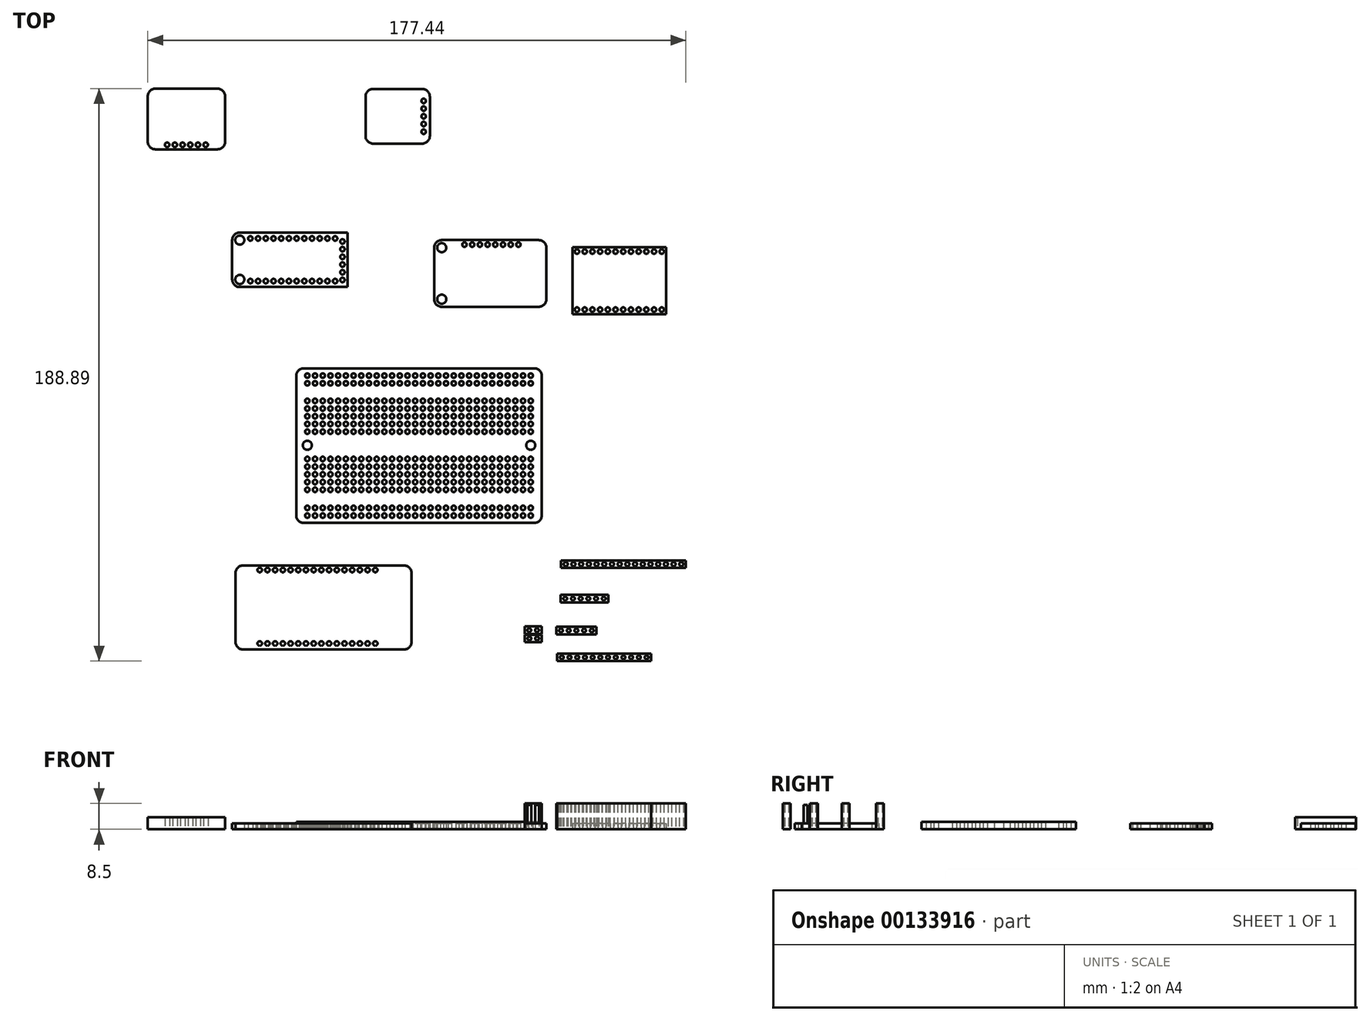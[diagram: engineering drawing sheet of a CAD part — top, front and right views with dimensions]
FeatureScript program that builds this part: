
annotation { "Feature Type Name" : "Feature", "Feature Type Description" : "" }
export const myFeature = defineFeature(function(context is Context, id is Id, definition is map)
    precondition{}
    {
        {
            var Q0;
            Q0=qCreatedBy(makeId("Top.planeOp"),FACE);
            var sketch = newSketch(context, id + "F0", { "sketchPlane" : qUnion([Q0])});
            skLineSegment(sketch, "E0.bottom", {"start": v(-38.07, -25.59) * mm, "end": v(42.93, -25.59) * mm});
            skLineSegment(sketch, "E0.top", {"start": v(-38.07, 25.41) * mm, "end": v(42.93, 25.41) * mm});
            skLineSegment(sketch, "E0.left", {"start": v(-38.07, -25.59) * mm, "end": v(-38.07, 25.41) * mm});
            skLineSegment(sketch, "E0.right", {"start": v(42.93, -25.59) * mm, "end": v(42.93, 25.41) * mm});
            skCircle(sketch, "E1", {"center": v(-34.4, -23.19) * mm, "radius": 0.75 * mm});
            skCircle(sketch, "E2.0.1.0", {"center": v(-34.4, -20.65) * mm, "radius": 0.75 * mm});
            skCircle(sketch, "E2.1.0.0", {"center": v(-31.86, -23.19) * mm, "radius": 0.75 * mm});
            skCircle(sketch, "E2.1.1.0", {"center": v(-31.86, -20.65) * mm, "radius": 0.75 * mm});
            skCircle(sketch, "E2.2.0.0", {"center": v(-29.32, -23.19) * mm, "radius": 0.75 * mm});
            skCircle(sketch, "E2.2.1.0", {"center": v(-29.32, -20.65) * mm, "radius": 0.75 * mm});
            skCircle(sketch, "E2.3.0.0", {"center": v(-26.78, -23.19) * mm, "radius": 0.75 * mm});
            skCircle(sketch, "E2.3.1.0", {"center": v(-26.78, -20.65) * mm, "radius": 0.75 * mm});
            skCircle(sketch, "E2.4.0.0", {"center": v(-24.24, -23.19) * mm, "radius": 0.75 * mm});
            skCircle(sketch, "E2.4.1.0", {"center": v(-24.24, -20.65) * mm, "radius": 0.75 * mm});
            skCircle(sketch, "E2.5.0.0", {"center": v(-21.7, -23.19) * mm, "radius": 0.75 * mm});
            skCircle(sketch, "E2.5.1.0", {"center": v(-21.7, -20.65) * mm, "radius": 0.75 * mm});
            skCircle(sketch, "E2.6.0.0", {"center": v(-19.16, -23.19) * mm, "radius": 0.75 * mm});
            skCircle(sketch, "E2.6.1.0", {"center": v(-19.16, -20.65) * mm, "radius": 0.75 * mm});
            skCircle(sketch, "E2.7.0.0", {"center": v(-16.62, -23.19) * mm, "radius": 0.75 * mm});
            skCircle(sketch, "E2.7.1.0", {"center": v(-16.62, -20.65) * mm, "radius": 0.75 * mm});
            skCircle(sketch, "E2.8.0.0", {"center": v(-14.08, -23.19) * mm, "radius": 0.75 * mm});
            skCircle(sketch, "E2.8.1.0", {"center": v(-14.08, -20.65) * mm, "radius": 0.75 * mm});
            skCircle(sketch, "E2.9.0.0", {"center": v(-11.54, -23.19) * mm, "radius": 0.75 * mm});
            skCircle(sketch, "E2.9.1.0", {"center": v(-11.54, -20.65) * mm, "radius": 0.75 * mm});
            skCircle(sketch, "E2.10.0.0", {"center": v(-9, -23.19) * mm, "radius": 0.75 * mm});
            skCircle(sketch, "E2.10.1.0", {"center": v(-9, -20.65) * mm, "radius": 0.75 * mm});
            skCircle(sketch, "E2.11.0.0", {"center": v(-6.46, -23.19) * mm, "radius": 0.75 * mm});
            skCircle(sketch, "E2.11.1.0", {"center": v(-6.46, -20.65) * mm, "radius": 0.75 * mm});
            skCircle(sketch, "E2.12.0.0", {"center": v(-3.92, -23.19) * mm, "radius": 0.75 * mm});
            skCircle(sketch, "E2.12.1.0", {"center": v(-3.92, -20.65) * mm, "radius": 0.75 * mm});
            skCircle(sketch, "E2.13.0.0", {"center": v(-1.38, -23.19) * mm, "radius": 0.75 * mm});
            skCircle(sketch, "E2.13.1.0", {"center": v(-1.38, -20.65) * mm, "radius": 0.75 * mm});
            skCircle(sketch, "E2.14.0.0", {"center": v(1.16, -23.19) * mm, "radius": 0.75 * mm});
            skCircle(sketch, "E2.14.1.0", {"center": v(1.16, -20.65) * mm, "radius": 0.75 * mm});
            skCircle(sketch, "E2.15.0.0", {"center": v(3.7, -23.19) * mm, "radius": 0.75 * mm});
            skCircle(sketch, "E2.15.1.0", {"center": v(3.7, -20.65) * mm, "radius": 0.75 * mm});
            skCircle(sketch, "E2.16.0.0", {"center": v(6.24, -23.19) * mm, "radius": 0.75 * mm});
            skCircle(sketch, "E2.16.1.0", {"center": v(6.24, -20.65) * mm, "radius": 0.75 * mm});
            skCircle(sketch, "E2.17.0.0", {"center": v(8.78, -23.19) * mm, "radius": 0.75 * mm});
            skCircle(sketch, "E2.17.1.0", {"center": v(8.78, -20.65) * mm, "radius": 0.75 * mm});
            skCircle(sketch, "E2.18.0.0", {"center": v(11.32, -23.19) * mm, "radius": 0.75 * mm});
            skCircle(sketch, "E2.18.1.0", {"center": v(11.32, -20.65) * mm, "radius": 0.75 * mm});
            skCircle(sketch, "E2.19.0.0", {"center": v(13.86, -23.19) * mm, "radius": 0.75 * mm});
            skCircle(sketch, "E2.19.1.0", {"center": v(13.86, -20.65) * mm, "radius": 0.75 * mm});
            skCircle(sketch, "E2.20.0.0", {"center": v(16.4, -23.19) * mm, "radius": 0.75 * mm});
            skCircle(sketch, "E2.20.1.0", {"center": v(16.4, -20.65) * mm, "radius": 0.75 * mm});
            skCircle(sketch, "E2.21.0.0", {"center": v(18.94, -23.19) * mm, "radius": 0.75 * mm});
            skCircle(sketch, "E2.21.1.0", {"center": v(18.94, -20.65) * mm, "radius": 0.75 * mm});
            skCircle(sketch, "E2.22.0.0", {"center": v(21.48, -23.19) * mm, "radius": 0.75 * mm});
            skCircle(sketch, "E2.22.1.0", {"center": v(21.48, -20.65) * mm, "radius": 0.75 * mm});
            skCircle(sketch, "E2.23.0.0", {"center": v(24.02, -23.19) * mm, "radius": 0.75 * mm});
            skCircle(sketch, "E2.23.1.0", {"center": v(24.02, -20.65) * mm, "radius": 0.75 * mm});
            skCircle(sketch, "E2.24.0.0", {"center": v(26.56, -23.19) * mm, "radius": 0.75 * mm});
            skCircle(sketch, "E2.24.1.0", {"center": v(26.56, -20.65) * mm, "radius": 0.75 * mm});
            skCircle(sketch, "E2.25.0.0", {"center": v(29.1, -23.19) * mm, "radius": 0.75 * mm});
            skCircle(sketch, "E2.25.1.0", {"center": v(29.1, -20.65) * mm, "radius": 0.75 * mm});
            skCircle(sketch, "E2.26.0.0", {"center": v(31.64, -23.19) * mm, "radius": 0.75 * mm});
            skCircle(sketch, "E2.26.1.0", {"center": v(31.64, -20.65) * mm, "radius": 0.75 * mm});
            skCircle(sketch, "E2.27.0.0", {"center": v(34.18, -23.19) * mm, "radius": 0.75 * mm});
            skCircle(sketch, "E2.27.1.0", {"center": v(34.18, -20.65) * mm, "radius": 0.75 * mm});
            skCircle(sketch, "E2.28.0.0", {"center": v(36.72, -23.19) * mm, "radius": 0.75 * mm});
            skCircle(sketch, "E2.28.1.0", {"center": v(36.72, -20.65) * mm, "radius": 0.75 * mm});
            skCircle(sketch, "E2.29.0.0", {"center": v(39.26, -23.19) * mm, "radius": 0.75 * mm});
            skCircle(sketch, "E2.29.1.0", {"center": v(39.26, -20.65) * mm, "radius": 0.75 * mm});
            skLineSegment(sketch, "E2.direction1", {"start": v(-34.4, -23.19) * mm, "end": v(-31.86, -23.19) * mm, "construction": true});
            skLineSegment(sketch, "E2.direction2", {"start": v(-34.4, -23.19) * mm, "end": v(-34.4, -20.65) * mm, "construction": true});
            skCircle(sketch, "E3", {"center": v(-34.4, 23.01) * mm, "radius": 0.75 * mm});
            skCircle(sketch, "E4.0.1.0", {"center": v(-34.4, 20.47) * mm, "radius": 0.75 * mm});
            skCircle(sketch, "E4.1.0.0", {"center": v(-31.86, 23.01) * mm, "radius": 0.75 * mm});
            skCircle(sketch, "E4.1.1.0", {"center": v(-31.86, 20.47) * mm, "radius": 0.75 * mm});
            skCircle(sketch, "E4.2.0.0", {"center": v(-29.32, 23.01) * mm, "radius": 0.75 * mm});
            skCircle(sketch, "E4.2.1.0", {"center": v(-29.32, 20.47) * mm, "radius": 0.75 * mm});
            skCircle(sketch, "E4.3.0.0", {"center": v(-26.78, 23.01) * mm, "radius": 0.75 * mm});
            skCircle(sketch, "E4.3.1.0", {"center": v(-26.78, 20.47) * mm, "radius": 0.75 * mm});
            skCircle(sketch, "E4.4.0.0", {"center": v(-24.24, 23.01) * mm, "radius": 0.75 * mm});
            skCircle(sketch, "E4.4.1.0", {"center": v(-24.24, 20.47) * mm, "radius": 0.75 * mm});
            skCircle(sketch, "E4.5.0.0", {"center": v(-21.7, 23.01) * mm, "radius": 0.75 * mm});
            skCircle(sketch, "E4.5.1.0", {"center": v(-21.7, 20.47) * mm, "radius": 0.75 * mm});
            skCircle(sketch, "E4.6.0.0", {"center": v(-19.16, 23.01) * mm, "radius": 0.75 * mm});
            skCircle(sketch, "E4.6.1.0", {"center": v(-19.16, 20.47) * mm, "radius": 0.75 * mm});
            skCircle(sketch, "E4.7.0.0", {"center": v(-16.62, 23.01) * mm, "radius": 0.75 * mm});
            skCircle(sketch, "E4.7.1.0", {"center": v(-16.62, 20.47) * mm, "radius": 0.75 * mm});
            skCircle(sketch, "E4.8.0.0", {"center": v(-14.08, 23.01) * mm, "radius": 0.75 * mm});
            skCircle(sketch, "E4.8.1.0", {"center": v(-14.08, 20.47) * mm, "radius": 0.75 * mm});
            skCircle(sketch, "E4.9.0.0", {"center": v(-11.54, 23.01) * mm, "radius": 0.75 * mm});
            skCircle(sketch, "E4.9.1.0", {"center": v(-11.54, 20.47) * mm, "radius": 0.75 * mm});
            skCircle(sketch, "E4.10.0.0", {"center": v(-9, 23.01) * mm, "radius": 0.75 * mm});
            skCircle(sketch, "E4.10.1.0", {"center": v(-9, 20.47) * mm, "radius": 0.75 * mm});
            skCircle(sketch, "E4.11.0.0", {"center": v(-6.46, 23.01) * mm, "radius": 0.75 * mm});
            skCircle(sketch, "E4.11.1.0", {"center": v(-6.46, 20.47) * mm, "radius": 0.75 * mm});
            skCircle(sketch, "E4.12.0.0", {"center": v(-3.92, 23.01) * mm, "radius": 0.75 * mm});
            skCircle(sketch, "E4.12.1.0", {"center": v(-3.92, 20.47) * mm, "radius": 0.75 * mm});
            skCircle(sketch, "E4.13.0.0", {"center": v(-1.38, 23.01) * mm, "radius": 0.75 * mm});
            skCircle(sketch, "E4.13.1.0", {"center": v(-1.38, 20.47) * mm, "radius": 0.75 * mm});
            skCircle(sketch, "E4.14.0.0", {"center": v(1.16, 23.01) * mm, "radius": 0.75 * mm});
            skCircle(sketch, "E4.14.1.0", {"center": v(1.16, 20.47) * mm, "radius": 0.75 * mm});
            skCircle(sketch, "E4.15.0.0", {"center": v(3.7, 23.01) * mm, "radius": 0.75 * mm});
            skCircle(sketch, "E4.15.1.0", {"center": v(3.7, 20.47) * mm, "radius": 0.75 * mm});
            skCircle(sketch, "E4.16.0.0", {"center": v(6.24, 23.01) * mm, "radius": 0.75 * mm});
            skCircle(sketch, "E4.16.1.0", {"center": v(6.24, 20.47) * mm, "radius": 0.75 * mm});
            skCircle(sketch, "E4.17.0.0", {"center": v(8.78, 23.01) * mm, "radius": 0.75 * mm});
            skCircle(sketch, "E4.17.1.0", {"center": v(8.78, 20.47) * mm, "radius": 0.75 * mm});
            skCircle(sketch, "E4.18.0.0", {"center": v(11.32, 23.01) * mm, "radius": 0.75 * mm});
            skCircle(sketch, "E4.18.1.0", {"center": v(11.32, 20.47) * mm, "radius": 0.75 * mm});
            skCircle(sketch, "E4.19.0.0", {"center": v(13.86, 23.01) * mm, "radius": 0.75 * mm});
            skCircle(sketch, "E4.19.1.0", {"center": v(13.86, 20.47) * mm, "radius": 0.75 * mm});
            skCircle(sketch, "E4.20.0.0", {"center": v(16.4, 23.01) * mm, "radius": 0.75 * mm});
            skCircle(sketch, "E4.20.1.0", {"center": v(16.4, 20.47) * mm, "radius": 0.75 * mm});
            skCircle(sketch, "E4.21.0.0", {"center": v(18.94, 23.01) * mm, "radius": 0.75 * mm});
            skCircle(sketch, "E4.21.1.0", {"center": v(18.94, 20.47) * mm, "radius": 0.75 * mm});
            skCircle(sketch, "E4.22.0.0", {"center": v(21.48, 23.01) * mm, "radius": 0.75 * mm});
            skCircle(sketch, "E4.22.1.0", {"center": v(21.48, 20.47) * mm, "radius": 0.75 * mm});
            skCircle(sketch, "E4.23.0.0", {"center": v(24.02, 23.01) * mm, "radius": 0.75 * mm});
            skCircle(sketch, "E4.23.1.0", {"center": v(24.02, 20.47) * mm, "radius": 0.75 * mm});
            skCircle(sketch, "E4.24.0.0", {"center": v(26.56, 23.01) * mm, "radius": 0.75 * mm});
            skCircle(sketch, "E4.24.1.0", {"center": v(26.56, 20.47) * mm, "radius": 0.75 * mm});
            skCircle(sketch, "E4.25.0.0", {"center": v(29.1, 23.01) * mm, "radius": 0.75 * mm});
            skCircle(sketch, "E4.25.1.0", {"center": v(29.1, 20.47) * mm, "radius": 0.75 * mm});
            skCircle(sketch, "E4.26.0.0", {"center": v(31.64, 23.01) * mm, "radius": 0.75 * mm});
            skCircle(sketch, "E4.26.1.0", {"center": v(31.64, 20.47) * mm, "radius": 0.75 * mm});
            skCircle(sketch, "E4.27.0.0", {"center": v(34.18, 23.01) * mm, "radius": 0.75 * mm});
            skCircle(sketch, "E4.27.1.0", {"center": v(34.18, 20.47) * mm, "radius": 0.75 * mm});
            skCircle(sketch, "E4.28.0.0", {"center": v(36.72, 23.01) * mm, "radius": 0.75 * mm});
            skCircle(sketch, "E4.28.1.0", {"center": v(36.72, 20.47) * mm, "radius": 0.75 * mm});
            skCircle(sketch, "E4.29.0.0", {"center": v(39.26, 23.01) * mm, "radius": 0.75 * mm});
            skCircle(sketch, "E4.29.1.0", {"center": v(39.26, 20.47) * mm, "radius": 0.75 * mm});
            skLineSegment(sketch, "E4.direction1", {"start": v(-34.4, 23.01) * mm, "end": v(-31.86, 23.01) * mm, "construction": true});
            skLineSegment(sketch, "E4.direction2", {"start": v(-34.4, 23.01) * mm, "end": v(-34.4, 20.47) * mm, "construction": true});
            skLineSegment(sketch, "E5", {"start": v(-38.07, 0) * mm, "end": v(42.93, -0.09) * mm, "construction": true});
            skLineSegment(sketch, "E6", {"start": v(-34.4, 20.47) * mm, "end": v(-34.4, -20.65) * mm, "construction": true});
            skLineSegment(sketch, "E7", {"start": v(-34.4, 0) * mm, "end": v(-34.4, 4.5) * mm, "construction": true});
            skCircle(sketch, "E8", {"center": v(-34.4, 4.5) * mm, "radius": 0.75 * mm});
            skCircle(sketch, "E9.0.1.0", {"center": v(-34.4, 7.04) * mm, "radius": 0.75 * mm});
            skCircle(sketch, "E9.0.2.0", {"center": v(-34.4, 9.58) * mm, "radius": 0.75 * mm});
            skCircle(sketch, "E9.0.3.0", {"center": v(-34.4, 12.12) * mm, "radius": 0.75 * mm});
            skCircle(sketch, "E9.0.4.0", {"center": v(-34.4, 14.66) * mm, "radius": 0.75 * mm});
            skCircle(sketch, "E9.1.0.0", {"center": v(-31.86, 4.5) * mm, "radius": 0.75 * mm});
            skCircle(sketch, "E9.1.1.0", {"center": v(-31.86, 7.04) * mm, "radius": 0.75 * mm});
            skCircle(sketch, "E9.1.2.0", {"center": v(-31.86, 9.58) * mm, "radius": 0.75 * mm});
            skCircle(sketch, "E9.1.3.0", {"center": v(-31.86, 12.12) * mm, "radius": 0.75 * mm});
            skCircle(sketch, "E9.1.4.0", {"center": v(-31.86, 14.66) * mm, "radius": 0.75 * mm});
            skCircle(sketch, "E9.2.0.0", {"center": v(-29.32, 4.5) * mm, "radius": 0.75 * mm});
            skCircle(sketch, "E9.2.1.0", {"center": v(-29.32, 7.04) * mm, "radius": 0.75 * mm});
            skCircle(sketch, "E9.2.2.0", {"center": v(-29.32, 9.58) * mm, "radius": 0.75 * mm});
            skCircle(sketch, "E9.2.3.0", {"center": v(-29.32, 12.12) * mm, "radius": 0.75 * mm});
            skCircle(sketch, "E9.2.4.0", {"center": v(-29.32, 14.66) * mm, "radius": 0.75 * mm});
            skCircle(sketch, "E9.3.0.0", {"center": v(-26.78, 4.5) * mm, "radius": 0.75 * mm});
            skCircle(sketch, "E9.3.1.0", {"center": v(-26.78, 7.04) * mm, "radius": 0.75 * mm});
            skCircle(sketch, "E9.3.2.0", {"center": v(-26.78, 9.58) * mm, "radius": 0.75 * mm});
            skCircle(sketch, "E9.3.3.0", {"center": v(-26.78, 12.12) * mm, "radius": 0.75 * mm});
            skCircle(sketch, "E9.3.4.0", {"center": v(-26.78, 14.66) * mm, "radius": 0.75 * mm});
            skCircle(sketch, "E9.4.0.0", {"center": v(-24.24, 4.5) * mm, "radius": 0.75 * mm});
            skCircle(sketch, "E9.4.1.0", {"center": v(-24.24, 7.04) * mm, "radius": 0.75 * mm});
            skCircle(sketch, "E9.4.2.0", {"center": v(-24.24, 9.58) * mm, "radius": 0.75 * mm});
            skCircle(sketch, "E9.4.3.0", {"center": v(-24.24, 12.12) * mm, "radius": 0.75 * mm});
            skCircle(sketch, "E9.4.4.0", {"center": v(-24.24, 14.66) * mm, "radius": 0.75 * mm});
            skCircle(sketch, "E9.5.0.0", {"center": v(-21.7, 4.5) * mm, "radius": 0.75 * mm});
            skCircle(sketch, "E9.5.1.0", {"center": v(-21.7, 7.04) * mm, "radius": 0.75 * mm});
            skCircle(sketch, "E9.5.2.0", {"center": v(-21.7, 9.58) * mm, "radius": 0.75 * mm});
            skCircle(sketch, "E9.5.3.0", {"center": v(-21.7, 12.12) * mm, "radius": 0.75 * mm});
            skCircle(sketch, "E9.5.4.0", {"center": v(-21.7, 14.66) * mm, "radius": 0.75 * mm});
            skCircle(sketch, "E9.6.0.0", {"center": v(-19.16, 4.5) * mm, "radius": 0.75 * mm});
            skCircle(sketch, "E9.6.1.0", {"center": v(-19.16, 7.04) * mm, "radius": 0.75 * mm});
            skCircle(sketch, "E9.6.2.0", {"center": v(-19.16, 9.58) * mm, "radius": 0.75 * mm});
            skCircle(sketch, "E9.6.3.0", {"center": v(-19.16, 12.12) * mm, "radius": 0.75 * mm});
            skCircle(sketch, "E9.6.4.0", {"center": v(-19.16, 14.66) * mm, "radius": 0.75 * mm});
            skCircle(sketch, "E9.7.0.0", {"center": v(-16.62, 4.5) * mm, "radius": 0.75 * mm});
            skCircle(sketch, "E9.7.1.0", {"center": v(-16.62, 7.04) * mm, "radius": 0.75 * mm});
            skCircle(sketch, "E9.7.2.0", {"center": v(-16.62, 9.58) * mm, "radius": 0.75 * mm});
            skCircle(sketch, "E9.7.3.0", {"center": v(-16.62, 12.12) * mm, "radius": 0.75 * mm});
            skCircle(sketch, "E9.7.4.0", {"center": v(-16.62, 14.66) * mm, "radius": 0.75 * mm});
            skCircle(sketch, "E9.8.0.0", {"center": v(-14.08, 4.5) * mm, "radius": 0.75 * mm});
            skCircle(sketch, "E9.8.1.0", {"center": v(-14.08, 7.04) * mm, "radius": 0.75 * mm});
            skCircle(sketch, "E9.8.2.0", {"center": v(-14.08, 9.58) * mm, "radius": 0.75 * mm});
            skCircle(sketch, "E9.8.3.0", {"center": v(-14.08, 12.12) * mm, "radius": 0.75 * mm});
            skCircle(sketch, "E9.8.4.0", {"center": v(-14.08, 14.66) * mm, "radius": 0.75 * mm});
            skCircle(sketch, "E9.9.0.0", {"center": v(-11.54, 4.5) * mm, "radius": 0.75 * mm});
            skCircle(sketch, "E9.9.1.0", {"center": v(-11.54, 7.04) * mm, "radius": 0.75 * mm});
            skCircle(sketch, "E9.9.2.0", {"center": v(-11.54, 9.58) * mm, "radius": 0.75 * mm});
            skCircle(sketch, "E9.9.3.0", {"center": v(-11.54, 12.12) * mm, "radius": 0.75 * mm});
            skCircle(sketch, "E9.9.4.0", {"center": v(-11.54, 14.66) * mm, "radius": 0.75 * mm});
            skCircle(sketch, "E9.10.0.0", {"center": v(-9, 4.5) * mm, "radius": 0.75 * mm});
            skCircle(sketch, "E9.10.1.0", {"center": v(-9, 7.04) * mm, "radius": 0.75 * mm});
            skCircle(sketch, "E9.10.2.0", {"center": v(-9, 9.58) * mm, "radius": 0.75 * mm});
            skCircle(sketch, "E9.10.3.0", {"center": v(-9, 12.12) * mm, "radius": 0.75 * mm});
            skCircle(sketch, "E9.10.4.0", {"center": v(-9, 14.66) * mm, "radius": 0.75 * mm});
            skCircle(sketch, "E9.11.0.0", {"center": v(-6.46, 4.5) * mm, "radius": 0.75 * mm});
            skCircle(sketch, "E9.11.1.0", {"center": v(-6.46, 7.04) * mm, "radius": 0.75 * mm});
            skCircle(sketch, "E9.11.2.0", {"center": v(-6.46, 9.58) * mm, "radius": 0.75 * mm});
            skCircle(sketch, "E9.11.3.0", {"center": v(-6.46, 12.12) * mm, "radius": 0.75 * mm});
            skCircle(sketch, "E9.11.4.0", {"center": v(-6.46, 14.66) * mm, "radius": 0.75 * mm});
            skCircle(sketch, "E9.12.0.0", {"center": v(-3.92, 4.5) * mm, "radius": 0.75 * mm});
            skCircle(sketch, "E9.12.1.0", {"center": v(-3.92, 7.04) * mm, "radius": 0.75 * mm});
            skCircle(sketch, "E9.12.2.0", {"center": v(-3.92, 9.58) * mm, "radius": 0.75 * mm});
            skCircle(sketch, "E9.12.3.0", {"center": v(-3.92, 12.12) * mm, "radius": 0.75 * mm});
            skCircle(sketch, "E9.12.4.0", {"center": v(-3.92, 14.66) * mm, "radius": 0.75 * mm});
            skCircle(sketch, "E9.13.0.0", {"center": v(-1.38, 4.5) * mm, "radius": 0.75 * mm});
            skCircle(sketch, "E9.13.1.0", {"center": v(-1.38, 7.04) * mm, "radius": 0.75 * mm});
            skCircle(sketch, "E9.13.2.0", {"center": v(-1.38, 9.58) * mm, "radius": 0.75 * mm});
            skCircle(sketch, "E9.13.3.0", {"center": v(-1.38, 12.12) * mm, "radius": 0.75 * mm});
            skCircle(sketch, "E9.13.4.0", {"center": v(-1.38, 14.66) * mm, "radius": 0.75 * mm});
            skCircle(sketch, "E9.14.0.0", {"center": v(1.16, 4.5) * mm, "radius": 0.75 * mm});
            skCircle(sketch, "E9.14.1.0", {"center": v(1.16, 7.04) * mm, "radius": 0.75 * mm});
            skCircle(sketch, "E9.14.2.0", {"center": v(1.16, 9.58) * mm, "radius": 0.75 * mm});
            skCircle(sketch, "E9.14.3.0", {"center": v(1.16, 12.12) * mm, "radius": 0.75 * mm});
            skCircle(sketch, "E9.14.4.0", {"center": v(1.16, 14.66) * mm, "radius": 0.75 * mm});
            skCircle(sketch, "E9.15.0.0", {"center": v(3.7, 4.5) * mm, "radius": 0.75 * mm});
            skCircle(sketch, "E9.15.1.0", {"center": v(3.7, 7.04) * mm, "radius": 0.75 * mm});
            skCircle(sketch, "E9.15.2.0", {"center": v(3.7, 9.58) * mm, "radius": 0.75 * mm});
            skCircle(sketch, "E9.15.3.0", {"center": v(3.7, 12.12) * mm, "radius": 0.75 * mm});
            skCircle(sketch, "E9.15.4.0", {"center": v(3.7, 14.66) * mm, "radius": 0.75 * mm});
            skCircle(sketch, "E9.16.0.0", {"center": v(6.24, 4.5) * mm, "radius": 0.75 * mm});
            skCircle(sketch, "E9.16.1.0", {"center": v(6.24, 7.04) * mm, "radius": 0.75 * mm});
            skCircle(sketch, "E9.16.2.0", {"center": v(6.24, 9.58) * mm, "radius": 0.75 * mm});
            skCircle(sketch, "E9.16.3.0", {"center": v(6.24, 12.12) * mm, "radius": 0.75 * mm});
            skCircle(sketch, "E9.16.4.0", {"center": v(6.24, 14.66) * mm, "radius": 0.75 * mm});
            skCircle(sketch, "E9.17.0.0", {"center": v(8.78, 4.5) * mm, "radius": 0.75 * mm});
            skCircle(sketch, "E9.17.1.0", {"center": v(8.78, 7.04) * mm, "radius": 0.75 * mm});
            skCircle(sketch, "E9.17.2.0", {"center": v(8.78, 9.58) * mm, "radius": 0.75 * mm});
            skCircle(sketch, "E9.17.3.0", {"center": v(8.78, 12.12) * mm, "radius": 0.75 * mm});
            skCircle(sketch, "E9.17.4.0", {"center": v(8.78, 14.66) * mm, "radius": 0.75 * mm});
            skCircle(sketch, "E9.18.0.0", {"center": v(11.32, 4.5) * mm, "radius": 0.75 * mm});
            skCircle(sketch, "E9.18.1.0", {"center": v(11.32, 7.04) * mm, "radius": 0.75 * mm});
            skCircle(sketch, "E9.18.2.0", {"center": v(11.32, 9.58) * mm, "radius": 0.75 * mm});
            skCircle(sketch, "E9.18.3.0", {"center": v(11.32, 12.12) * mm, "radius": 0.75 * mm});
            skCircle(sketch, "E9.18.4.0", {"center": v(11.32, 14.66) * mm, "radius": 0.75 * mm});
            skCircle(sketch, "E9.19.0.0", {"center": v(13.86, 4.5) * mm, "radius": 0.75 * mm});
            skCircle(sketch, "E9.19.1.0", {"center": v(13.86, 7.04) * mm, "radius": 0.75 * mm});
            skCircle(sketch, "E9.19.2.0", {"center": v(13.86, 9.58) * mm, "radius": 0.75 * mm});
            skCircle(sketch, "E9.19.3.0", {"center": v(13.86, 12.12) * mm, "radius": 0.75 * mm});
            skCircle(sketch, "E9.19.4.0", {"center": v(13.86, 14.66) * mm, "radius": 0.75 * mm});
            skCircle(sketch, "E9.20.0.0", {"center": v(16.4, 4.5) * mm, "radius": 0.75 * mm});
            skCircle(sketch, "E9.20.1.0", {"center": v(16.4, 7.04) * mm, "radius": 0.75 * mm});
            skCircle(sketch, "E9.20.2.0", {"center": v(16.4, 9.58) * mm, "radius": 0.75 * mm});
            skCircle(sketch, "E9.20.3.0", {"center": v(16.4, 12.12) * mm, "radius": 0.75 * mm});
            skCircle(sketch, "E9.20.4.0", {"center": v(16.4, 14.66) * mm, "radius": 0.75 * mm});
            skCircle(sketch, "E9.21.0.0", {"center": v(18.94, 4.5) * mm, "radius": 0.75 * mm});
            skCircle(sketch, "E9.21.1.0", {"center": v(18.94, 7.04) * mm, "radius": 0.75 * mm});
            skCircle(sketch, "E9.21.2.0", {"center": v(18.94, 9.58) * mm, "radius": 0.75 * mm});
            skCircle(sketch, "E9.21.3.0", {"center": v(18.94, 12.12) * mm, "radius": 0.75 * mm});
            skCircle(sketch, "E9.21.4.0", {"center": v(18.94, 14.66) * mm, "radius": 0.75 * mm});
            skCircle(sketch, "E9.22.0.0", {"center": v(21.48, 4.5) * mm, "radius": 0.75 * mm});
            skCircle(sketch, "E9.22.1.0", {"center": v(21.48, 7.04) * mm, "radius": 0.75 * mm});
            skCircle(sketch, "E9.22.2.0", {"center": v(21.48, 9.58) * mm, "radius": 0.75 * mm});
            skCircle(sketch, "E9.22.3.0", {"center": v(21.48, 12.12) * mm, "radius": 0.75 * mm});
            skCircle(sketch, "E9.22.4.0", {"center": v(21.48, 14.66) * mm, "radius": 0.75 * mm});
            skCircle(sketch, "E9.23.0.0", {"center": v(24.02, 4.5) * mm, "radius": 0.75 * mm});
            skCircle(sketch, "E9.23.1.0", {"center": v(24.02, 7.04) * mm, "radius": 0.75 * mm});
            skCircle(sketch, "E9.23.2.0", {"center": v(24.02, 9.58) * mm, "radius": 0.75 * mm});
            skCircle(sketch, "E9.23.3.0", {"center": v(24.02, 12.12) * mm, "radius": 0.75 * mm});
            skCircle(sketch, "E9.23.4.0", {"center": v(24.02, 14.66) * mm, "radius": 0.75 * mm});
            skCircle(sketch, "E9.24.0.0", {"center": v(26.56, 4.5) * mm, "radius": 0.75 * mm});
            skCircle(sketch, "E9.24.1.0", {"center": v(26.56, 7.04) * mm, "radius": 0.75 * mm});
            skCircle(sketch, "E9.24.2.0", {"center": v(26.56, 9.58) * mm, "radius": 0.75 * mm});
            skCircle(sketch, "E9.24.3.0", {"center": v(26.56, 12.12) * mm, "radius": 0.75 * mm});
            skCircle(sketch, "E9.24.4.0", {"center": v(26.56, 14.66) * mm, "radius": 0.75 * mm});
            skCircle(sketch, "E9.25.0.0", {"center": v(29.1, 4.5) * mm, "radius": 0.75 * mm});
            skCircle(sketch, "E9.25.1.0", {"center": v(29.1, 7.04) * mm, "radius": 0.75 * mm});
            skCircle(sketch, "E9.25.2.0", {"center": v(29.1, 9.58) * mm, "radius": 0.75 * mm});
            skCircle(sketch, "E9.25.3.0", {"center": v(29.1, 12.12) * mm, "radius": 0.75 * mm});
            skCircle(sketch, "E9.25.4.0", {"center": v(29.1, 14.66) * mm, "radius": 0.75 * mm});
            skCircle(sketch, "E9.26.0.0", {"center": v(31.64, 4.5) * mm, "radius": 0.75 * mm});
            skCircle(sketch, "E9.26.1.0", {"center": v(31.64, 7.04) * mm, "radius": 0.75 * mm});
            skCircle(sketch, "E9.26.2.0", {"center": v(31.64, 9.58) * mm, "radius": 0.75 * mm});
            skCircle(sketch, "E9.26.3.0", {"center": v(31.64, 12.12) * mm, "radius": 0.75 * mm});
            skCircle(sketch, "E9.26.4.0", {"center": v(31.64, 14.66) * mm, "radius": 0.75 * mm});
            skCircle(sketch, "E9.27.0.0", {"center": v(34.18, 4.5) * mm, "radius": 0.75 * mm});
            skCircle(sketch, "E9.27.1.0", {"center": v(34.18, 7.04) * mm, "radius": 0.75 * mm});
            skCircle(sketch, "E9.27.2.0", {"center": v(34.18, 9.58) * mm, "radius": 0.75 * mm});
            skCircle(sketch, "E9.27.3.0", {"center": v(34.18, 12.12) * mm, "radius": 0.75 * mm});
            skCircle(sketch, "E9.27.4.0", {"center": v(34.18, 14.66) * mm, "radius": 0.75 * mm});
            skCircle(sketch, "E9.28.0.0", {"center": v(36.72, 4.5) * mm, "radius": 0.75 * mm});
            skCircle(sketch, "E9.28.1.0", {"center": v(36.72, 7.04) * mm, "radius": 0.75 * mm});
            skCircle(sketch, "E9.28.2.0", {"center": v(36.72, 9.58) * mm, "radius": 0.75 * mm});
            skCircle(sketch, "E9.28.3.0", {"center": v(36.72, 12.12) * mm, "radius": 0.75 * mm});
            skCircle(sketch, "E9.28.4.0", {"center": v(36.72, 14.66) * mm, "radius": 0.75 * mm});
            skCircle(sketch, "E9.29.0.0", {"center": v(39.26, 4.5) * mm, "radius": 0.75 * mm});
            skCircle(sketch, "E9.29.1.0", {"center": v(39.26, 7.04) * mm, "radius": 0.75 * mm});
            skCircle(sketch, "E9.29.2.0", {"center": v(39.26, 9.58) * mm, "radius": 0.75 * mm});
            skCircle(sketch, "E9.29.3.0", {"center": v(39.26, 12.12) * mm, "radius": 0.75 * mm});
            skCircle(sketch, "E9.29.4.0", {"center": v(39.26, 14.66) * mm, "radius": 0.75 * mm});
            skLineSegment(sketch, "E9.direction1", {"start": v(-34.4, 4.5) * mm, "end": v(-31.86, 4.5) * mm, "construction": true});
            skLineSegment(sketch, "E9.direction2", {"start": v(-34.4, 4.5) * mm, "end": v(-34.4, 7.04) * mm, "construction": true});
            skLineSegment(sketch, "E10", {"start": v(-34.4, 0) * mm, "end": v(-34.4, -4.5) * mm, "construction": true});
            skCircle(sketch, "E11", {"center": v(-34.4, -4.5) * mm, "radius": 0.75 * mm});
            skCircle(sketch, "E12.0.1.0", {"center": v(-34.4, -7.04) * mm, "radius": 0.75 * mm});
            skCircle(sketch, "E12.0.2.0", {"center": v(-34.4, -9.58) * mm, "radius": 0.75 * mm});
            skCircle(sketch, "E12.0.3.0", {"center": v(-34.4, -12.12) * mm, "radius": 0.75 * mm});
            skCircle(sketch, "E12.0.4.0", {"center": v(-34.4, -14.66) * mm, "radius": 0.75 * mm});
            skCircle(sketch, "E12.1.0.0", {"center": v(-31.86, -4.5) * mm, "radius": 0.75 * mm});
            skCircle(sketch, "E12.1.1.0", {"center": v(-31.86, -7.04) * mm, "radius": 0.75 * mm});
            skCircle(sketch, "E12.1.2.0", {"center": v(-31.86, -9.58) * mm, "radius": 0.75 * mm});
            skCircle(sketch, "E12.1.3.0", {"center": v(-31.86, -12.12) * mm, "radius": 0.75 * mm});
            skCircle(sketch, "E12.1.4.0", {"center": v(-31.86, -14.66) * mm, "radius": 0.75 * mm});
            skCircle(sketch, "E12.2.0.0", {"center": v(-29.32, -4.5) * mm, "radius": 0.75 * mm});
            skCircle(sketch, "E12.2.1.0", {"center": v(-29.32, -7.04) * mm, "radius": 0.75 * mm});
            skCircle(sketch, "E12.2.2.0", {"center": v(-29.32, -9.58) * mm, "radius": 0.75 * mm});
            skCircle(sketch, "E12.2.3.0", {"center": v(-29.32, -12.12) * mm, "radius": 0.75 * mm});
            skCircle(sketch, "E12.2.4.0", {"center": v(-29.32, -14.66) * mm, "radius": 0.75 * mm});
            skCircle(sketch, "E12.3.0.0", {"center": v(-26.78, -4.5) * mm, "radius": 0.75 * mm});
            skCircle(sketch, "E12.3.1.0", {"center": v(-26.78, -7.04) * mm, "radius": 0.75 * mm});
            skCircle(sketch, "E12.3.2.0", {"center": v(-26.78, -9.58) * mm, "radius": 0.75 * mm});
            skCircle(sketch, "E12.3.3.0", {"center": v(-26.78, -12.12) * mm, "radius": 0.75 * mm});
            skCircle(sketch, "E12.3.4.0", {"center": v(-26.78, -14.66) * mm, "radius": 0.75 * mm});
            skCircle(sketch, "E12.4.0.0", {"center": v(-24.24, -4.5) * mm, "radius": 0.75 * mm});
            skCircle(sketch, "E12.4.1.0", {"center": v(-24.24, -7.04) * mm, "radius": 0.75 * mm});
            skCircle(sketch, "E12.4.2.0", {"center": v(-24.24, -9.58) * mm, "radius": 0.75 * mm});
            skCircle(sketch, "E12.4.3.0", {"center": v(-24.24, -12.12) * mm, "radius": 0.75 * mm});
            skCircle(sketch, "E12.4.4.0", {"center": v(-24.24, -14.66) * mm, "radius": 0.75 * mm});
            skCircle(sketch, "E12.5.0.0", {"center": v(-21.7, -4.5) * mm, "radius": 0.75 * mm});
            skCircle(sketch, "E12.5.1.0", {"center": v(-21.7, -7.04) * mm, "radius": 0.75 * mm});
            skCircle(sketch, "E12.5.2.0", {"center": v(-21.7, -9.58) * mm, "radius": 0.75 * mm});
            skCircle(sketch, "E12.5.3.0", {"center": v(-21.7, -12.12) * mm, "radius": 0.75 * mm});
            skCircle(sketch, "E12.5.4.0", {"center": v(-21.7, -14.66) * mm, "radius": 0.75 * mm});
            skCircle(sketch, "E12.6.0.0", {"center": v(-19.16, -4.5) * mm, "radius": 0.75 * mm});
            skCircle(sketch, "E12.6.1.0", {"center": v(-19.16, -7.04) * mm, "radius": 0.75 * mm});
            skCircle(sketch, "E12.6.2.0", {"center": v(-19.16, -9.58) * mm, "radius": 0.75 * mm});
            skCircle(sketch, "E12.6.3.0", {"center": v(-19.16, -12.12) * mm, "radius": 0.75 * mm});
            skCircle(sketch, "E12.6.4.0", {"center": v(-19.16, -14.66) * mm, "radius": 0.75 * mm});
            skCircle(sketch, "E12.7.0.0", {"center": v(-16.62, -4.5) * mm, "radius": 0.75 * mm});
            skCircle(sketch, "E12.7.1.0", {"center": v(-16.62, -7.04) * mm, "radius": 0.75 * mm});
            skCircle(sketch, "E12.7.2.0", {"center": v(-16.62, -9.58) * mm, "radius": 0.75 * mm});
            skCircle(sketch, "E12.7.3.0", {"center": v(-16.62, -12.12) * mm, "radius": 0.75 * mm});
            skCircle(sketch, "E12.7.4.0", {"center": v(-16.62, -14.66) * mm, "radius": 0.75 * mm});
            skCircle(sketch, "E12.8.0.0", {"center": v(-14.08, -4.5) * mm, "radius": 0.75 * mm});
            skCircle(sketch, "E12.8.1.0", {"center": v(-14.08, -7.04) * mm, "radius": 0.75 * mm});
            skCircle(sketch, "E12.8.2.0", {"center": v(-14.08, -9.58) * mm, "radius": 0.75 * mm});
            skCircle(sketch, "E12.8.3.0", {"center": v(-14.08, -12.12) * mm, "radius": 0.75 * mm});
            skCircle(sketch, "E12.8.4.0", {"center": v(-14.08, -14.66) * mm, "radius": 0.75 * mm});
            skCircle(sketch, "E12.9.0.0", {"center": v(-11.54, -4.5) * mm, "radius": 0.75 * mm});
            skCircle(sketch, "E12.9.1.0", {"center": v(-11.54, -7.04) * mm, "radius": 0.75 * mm});
            skCircle(sketch, "E12.9.2.0", {"center": v(-11.54, -9.58) * mm, "radius": 0.75 * mm});
            skCircle(sketch, "E12.9.3.0", {"center": v(-11.54, -12.12) * mm, "radius": 0.75 * mm});
            skCircle(sketch, "E12.9.4.0", {"center": v(-11.54, -14.66) * mm, "radius": 0.75 * mm});
            skCircle(sketch, "E12.10.0.0", {"center": v(-9, -4.5) * mm, "radius": 0.75 * mm});
            skCircle(sketch, "E12.10.1.0", {"center": v(-9, -7.04) * mm, "radius": 0.75 * mm});
            skCircle(sketch, "E12.10.2.0", {"center": v(-9, -9.58) * mm, "radius": 0.75 * mm});
            skCircle(sketch, "E12.10.3.0", {"center": v(-9, -12.12) * mm, "radius": 0.75 * mm});
            skCircle(sketch, "E12.10.4.0", {"center": v(-9, -14.66) * mm, "radius": 0.75 * mm});
            skCircle(sketch, "E12.11.0.0", {"center": v(-6.46, -4.5) * mm, "radius": 0.75 * mm});
            skCircle(sketch, "E12.11.1.0", {"center": v(-6.46, -7.04) * mm, "radius": 0.75 * mm});
            skCircle(sketch, "E12.11.2.0", {"center": v(-6.46, -9.58) * mm, "radius": 0.75 * mm});
            skCircle(sketch, "E12.11.3.0", {"center": v(-6.46, -12.12) * mm, "radius": 0.75 * mm});
            skCircle(sketch, "E12.11.4.0", {"center": v(-6.46, -14.66) * mm, "radius": 0.75 * mm});
            skCircle(sketch, "E12.12.0.0", {"center": v(-3.92, -4.5) * mm, "radius": 0.75 * mm});
            skCircle(sketch, "E12.12.1.0", {"center": v(-3.92, -7.04) * mm, "radius": 0.75 * mm});
            skCircle(sketch, "E12.12.2.0", {"center": v(-3.92, -9.58) * mm, "radius": 0.75 * mm});
            skCircle(sketch, "E12.12.3.0", {"center": v(-3.92, -12.12) * mm, "radius": 0.75 * mm});
            skCircle(sketch, "E12.12.4.0", {"center": v(-3.92, -14.66) * mm, "radius": 0.75 * mm});
            skCircle(sketch, "E12.13.0.0", {"center": v(-1.38, -4.5) * mm, "radius": 0.75 * mm});
            skCircle(sketch, "E12.13.1.0", {"center": v(-1.38, -7.04) * mm, "radius": 0.75 * mm});
            skCircle(sketch, "E12.13.2.0", {"center": v(-1.38, -9.58) * mm, "radius": 0.75 * mm});
            skCircle(sketch, "E12.13.3.0", {"center": v(-1.38, -12.12) * mm, "radius": 0.75 * mm});
            skCircle(sketch, "E12.13.4.0", {"center": v(-1.38, -14.66) * mm, "radius": 0.75 * mm});
            skCircle(sketch, "E12.14.0.0", {"center": v(1.16, -4.5) * mm, "radius": 0.75 * mm});
            skCircle(sketch, "E12.14.1.0", {"center": v(1.16, -7.04) * mm, "radius": 0.75 * mm});
            skCircle(sketch, "E12.14.2.0", {"center": v(1.16, -9.58) * mm, "radius": 0.75 * mm});
            skCircle(sketch, "E12.14.3.0", {"center": v(1.16, -12.12) * mm, "radius": 0.75 * mm});
            skCircle(sketch, "E12.14.4.0", {"center": v(1.16, -14.66) * mm, "radius": 0.75 * mm});
            skCircle(sketch, "E12.15.0.0", {"center": v(3.7, -4.5) * mm, "radius": 0.75 * mm});
            skCircle(sketch, "E12.15.1.0", {"center": v(3.7, -7.04) * mm, "radius": 0.75 * mm});
            skCircle(sketch, "E12.15.2.0", {"center": v(3.7, -9.58) * mm, "radius": 0.75 * mm});
            skCircle(sketch, "E12.15.3.0", {"center": v(3.7, -12.12) * mm, "radius": 0.75 * mm});
            skCircle(sketch, "E12.15.4.0", {"center": v(3.7, -14.66) * mm, "radius": 0.75 * mm});
            skCircle(sketch, "E12.16.0.0", {"center": v(6.24, -4.5) * mm, "radius": 0.75 * mm});
            skCircle(sketch, "E12.16.1.0", {"center": v(6.24, -7.04) * mm, "radius": 0.75 * mm});
            skCircle(sketch, "E12.16.2.0", {"center": v(6.24, -9.58) * mm, "radius": 0.75 * mm});
            skCircle(sketch, "E12.16.3.0", {"center": v(6.24, -12.12) * mm, "radius": 0.75 * mm});
            skCircle(sketch, "E12.16.4.0", {"center": v(6.24, -14.66) * mm, "radius": 0.75 * mm});
            skCircle(sketch, "E12.17.0.0", {"center": v(8.78, -4.5) * mm, "radius": 0.75 * mm});
            skCircle(sketch, "E12.17.1.0", {"center": v(8.78, -7.04) * mm, "radius": 0.75 * mm});
            skCircle(sketch, "E12.17.2.0", {"center": v(8.78, -9.58) * mm, "radius": 0.75 * mm});
            skCircle(sketch, "E12.17.3.0", {"center": v(8.78, -12.12) * mm, "radius": 0.75 * mm});
            skCircle(sketch, "E12.17.4.0", {"center": v(8.78, -14.66) * mm, "radius": 0.75 * mm});
            skCircle(sketch, "E12.18.0.0", {"center": v(11.32, -4.5) * mm, "radius": 0.75 * mm});
            skCircle(sketch, "E12.18.1.0", {"center": v(11.32, -7.04) * mm, "radius": 0.75 * mm});
            skCircle(sketch, "E12.18.2.0", {"center": v(11.32, -9.58) * mm, "radius": 0.75 * mm});
            skCircle(sketch, "E12.18.3.0", {"center": v(11.32, -12.12) * mm, "radius": 0.75 * mm});
            skCircle(sketch, "E12.18.4.0", {"center": v(11.32, -14.66) * mm, "radius": 0.75 * mm});
            skCircle(sketch, "E12.19.0.0", {"center": v(13.86, -4.5) * mm, "radius": 0.75 * mm});
            skCircle(sketch, "E12.19.1.0", {"center": v(13.86, -7.04) * mm, "radius": 0.75 * mm});
            skCircle(sketch, "E12.19.2.0", {"center": v(13.86, -9.58) * mm, "radius": 0.75 * mm});
            skCircle(sketch, "E12.19.3.0", {"center": v(13.86, -12.12) * mm, "radius": 0.75 * mm});
            skCircle(sketch, "E12.19.4.0", {"center": v(13.86, -14.66) * mm, "radius": 0.75 * mm});
            skCircle(sketch, "E12.20.0.0", {"center": v(16.4, -4.5) * mm, "radius": 0.75 * mm});
            skCircle(sketch, "E12.20.1.0", {"center": v(16.4, -7.04) * mm, "radius": 0.75 * mm});
            skCircle(sketch, "E12.20.2.0", {"center": v(16.4, -9.58) * mm, "radius": 0.75 * mm});
            skCircle(sketch, "E12.20.3.0", {"center": v(16.4, -12.12) * mm, "radius": 0.75 * mm});
            skCircle(sketch, "E12.20.4.0", {"center": v(16.4, -14.66) * mm, "radius": 0.75 * mm});
            skCircle(sketch, "E12.21.0.0", {"center": v(18.94, -4.5) * mm, "radius": 0.75 * mm});
            skCircle(sketch, "E12.21.1.0", {"center": v(18.94, -7.04) * mm, "radius": 0.75 * mm});
            skCircle(sketch, "E12.21.2.0", {"center": v(18.94, -9.58) * mm, "radius": 0.75 * mm});
            skCircle(sketch, "E12.21.3.0", {"center": v(18.94, -12.12) * mm, "radius": 0.75 * mm});
            skCircle(sketch, "E12.21.4.0", {"center": v(18.94, -14.66) * mm, "radius": 0.75 * mm});
            skCircle(sketch, "E12.22.0.0", {"center": v(21.48, -4.5) * mm, "radius": 0.75 * mm});
            skCircle(sketch, "E12.22.1.0", {"center": v(21.48, -7.04) * mm, "radius": 0.75 * mm});
            skCircle(sketch, "E12.22.2.0", {"center": v(21.48, -9.58) * mm, "radius": 0.75 * mm});
            skCircle(sketch, "E12.22.3.0", {"center": v(21.48, -12.12) * mm, "radius": 0.75 * mm});
            skCircle(sketch, "E12.22.4.0", {"center": v(21.48, -14.66) * mm, "radius": 0.75 * mm});
            skCircle(sketch, "E12.23.0.0", {"center": v(24.02, -4.5) * mm, "radius": 0.75 * mm});
            skCircle(sketch, "E12.23.1.0", {"center": v(24.02, -7.04) * mm, "radius": 0.75 * mm});
            skCircle(sketch, "E12.23.2.0", {"center": v(24.02, -9.58) * mm, "radius": 0.75 * mm});
            skCircle(sketch, "E12.23.3.0", {"center": v(24.02, -12.12) * mm, "radius": 0.75 * mm});
            skCircle(sketch, "E12.23.4.0", {"center": v(24.02, -14.66) * mm, "radius": 0.75 * mm});
            skCircle(sketch, "E12.24.0.0", {"center": v(26.56, -4.5) * mm, "radius": 0.75 * mm});
            skCircle(sketch, "E12.24.1.0", {"center": v(26.56, -7.04) * mm, "radius": 0.75 * mm});
            skCircle(sketch, "E12.24.2.0", {"center": v(26.56, -9.58) * mm, "radius": 0.75 * mm});
            skCircle(sketch, "E12.24.3.0", {"center": v(26.56, -12.12) * mm, "radius": 0.75 * mm});
            skCircle(sketch, "E12.24.4.0", {"center": v(26.56, -14.66) * mm, "radius": 0.75 * mm});
            skCircle(sketch, "E12.25.0.0", {"center": v(29.1, -4.5) * mm, "radius": 0.75 * mm});
            skCircle(sketch, "E12.25.1.0", {"center": v(29.1, -7.04) * mm, "radius": 0.75 * mm});
            skCircle(sketch, "E12.25.2.0", {"center": v(29.1, -9.58) * mm, "radius": 0.75 * mm});
            skCircle(sketch, "E12.25.3.0", {"center": v(29.1, -12.12) * mm, "radius": 0.75 * mm});
            skCircle(sketch, "E12.25.4.0", {"center": v(29.1, -14.66) * mm, "radius": 0.75 * mm});
            skCircle(sketch, "E12.26.0.0", {"center": v(31.64, -4.5) * mm, "radius": 0.75 * mm});
            skCircle(sketch, "E12.26.1.0", {"center": v(31.64, -7.04) * mm, "radius": 0.75 * mm});
            skCircle(sketch, "E12.26.2.0", {"center": v(31.64, -9.58) * mm, "radius": 0.75 * mm});
            skCircle(sketch, "E12.26.3.0", {"center": v(31.64, -12.12) * mm, "radius": 0.75 * mm});
            skCircle(sketch, "E12.26.4.0", {"center": v(31.64, -14.66) * mm, "radius": 0.75 * mm});
            skCircle(sketch, "E12.27.0.0", {"center": v(34.18, -4.5) * mm, "radius": 0.75 * mm});
            skCircle(sketch, "E12.27.1.0", {"center": v(34.18, -7.04) * mm, "radius": 0.75 * mm});
            skCircle(sketch, "E12.27.2.0", {"center": v(34.18, -9.58) * mm, "radius": 0.75 * mm});
            skCircle(sketch, "E12.27.3.0", {"center": v(34.18, -12.12) * mm, "radius": 0.75 * mm});
            skCircle(sketch, "E12.27.4.0", {"center": v(34.18, -14.66) * mm, "radius": 0.75 * mm});
            skCircle(sketch, "E12.28.0.0", {"center": v(36.72, -4.5) * mm, "radius": 0.75 * mm});
            skCircle(sketch, "E12.28.1.0", {"center": v(36.72, -7.04) * mm, "radius": 0.75 * mm});
            skCircle(sketch, "E12.28.2.0", {"center": v(36.72, -9.58) * mm, "radius": 0.75 * mm});
            skCircle(sketch, "E12.28.3.0", {"center": v(36.72, -12.12) * mm, "radius": 0.75 * mm});
            skCircle(sketch, "E12.28.4.0", {"center": v(36.72, -14.66) * mm, "radius": 0.75 * mm});
            skCircle(sketch, "E12.29.0.0", {"center": v(39.26, -4.5) * mm, "radius": 0.75 * mm});
            skCircle(sketch, "E12.29.1.0", {"center": v(39.26, -7.04) * mm, "radius": 0.75 * mm});
            skCircle(sketch, "E12.29.2.0", {"center": v(39.26, -9.58) * mm, "radius": 0.75 * mm});
            skCircle(sketch, "E12.29.3.0", {"center": v(39.26, -12.12) * mm, "radius": 0.75 * mm});
            skCircle(sketch, "E12.29.4.0", {"center": v(39.26, -14.66) * mm, "radius": 0.75 * mm});
            skLineSegment(sketch, "E12.direction1", {"start": v(-34.4, -4.5) * mm, "end": v(-31.86, -4.5) * mm, "construction": true});
            skLineSegment(sketch, "E12.direction2", {"start": v(-34.4, -4.5) * mm, "end": v(-34.4, -7.04) * mm, "construction": true});
            skLineSegment(sketch, "E13", {"start": v(39.26, 4.5) * mm, "end": v(39.26, -4.5) * mm, "construction": true});
            skCircle(sketch, "E14", {"center": v(39.26, 0) * mm, "radius": 1.5 * mm});
            skCircle(sketch, "E15", {"center": v(-34.4, 0) * mm, "radius": 1.5 * mm});
            skSolve(sketch);
        }
        {
            var Q0;
            Q0 = qSketchRegion(id + "F0", true);
            extrude(context, id + "F1", {"entities" : qUnion([Q0]), "depth" : 2.5 * mm});
        }
        {
            var Q0;
            Q0=makeQuery(id+"F1.opExtrude","SWEPT_EDGE",EDGE,{"disambiguationData":[OSD([sQuery(id+"F0.wireOp",EDGE,"E0.top"),sQuery(id+"F0.wireOp",EDGE,"E0.right")])]});
            var Q1;
            Q1=makeQuery(id+"F1.opExtrude","SWEPT_EDGE",EDGE,{"disambiguationData":[OSD([sQuery(id+"F0.wireOp",EDGE,"E0.bottom"),sQuery(id+"F0.wireOp",EDGE,"E0.right")])]});
            var Q2;
            Q2=makeQuery(id+"F1.opExtrude","SWEPT_EDGE",EDGE,{"disambiguationData":[OSD([sQuery(id+"F0.wireOp",EDGE,"E0.bottom"),sQuery(id+"F0.wireOp",EDGE,"E0.left")])]});
            var Q3;
            Q3=makeQuery(id+"F1.opExtrude","SWEPT_EDGE",EDGE,{"disambiguationData":[OSD([sQuery(id+"F0.wireOp",EDGE,"E0.top"),sQuery(id+"F0.wireOp",EDGE,"E0.left")])]});
            fillet(context, id + "F2", {"entities" : qUnion([Q0, Q1, Q2, Q3]), "radius" : 2.5 * mm, "tangentPropagation" : true, "allowEdgeOverflow" : false});
        }
        {
            var Q0;
            Q0=qCreatedBy(makeId("Top.planeOp"),FACE);
            var sketch = newSketch(context, id + "F3", { "sketchPlane" : qUnion([Q0])});
            skLineSegment(sketch, "E16.bottom", {"start": v(37.26, -59.75) * mm, "end": v(42.84, -59.75) * mm});
            skLineSegment(sketch, "E16.top", {"start": v(37.26, -62.25) * mm, "end": v(42.84, -62.25) * mm});
            skLineSegment(sketch, "E16.left", {"start": v(37.26, -59.75) * mm, "end": v(37.26, -62.25) * mm});
            skLineSegment(sketch, "E16.right", {"start": v(42.84, -59.75) * mm, "end": v(42.84, -62.25) * mm});
            skLineSegment(sketch, "E17", {"start": v(40.05, -59.75) * mm, "end": v(40.05, -62.25) * mm, "construction": true});
            skLineSegment(sketch, "E18", {"start": v(40.05, -61) * mm, "end": v(38.78, -61) * mm});
            skLineSegment(sketch, "E19.bottom", {"start": v(37.31, -62.48) * mm, "end": v(42.9, -62.48) * mm});
            skLineSegment(sketch, "E19.top", {"start": v(37.31, -64.98) * mm, "end": v(42.9, -64.98) * mm});
            skLineSegment(sketch, "E19.left", {"start": v(37.31, -62.48) * mm, "end": v(37.31, -64.98) * mm});
            skLineSegment(sketch, "E19.right", {"start": v(42.9, -62.48) * mm, "end": v(42.9, -64.98) * mm});
            skPoint(sketch, "E20.middle", {"position": v(38.83, -63.73) * mm});
            skLineSegment(sketch, "E21", {"start": v(40.1, -62.48) * mm, "end": v(40.1, -64.98) * mm, "construction": true});
            skLineSegment(sketch, "E22.bottom", {"start": v(47.73, -59.85) * mm, "end": v(60.93, -59.85) * mm});
            skLineSegment(sketch, "E22.top", {"start": v(47.73, -62.35) * mm, "end": v(60.93, -62.35) * mm});
            skLineSegment(sketch, "E22.left", {"start": v(47.73, -59.85) * mm, "end": v(47.73, -62.35) * mm});
            skLineSegment(sketch, "E22.right", {"start": v(60.93, -59.85) * mm, "end": v(60.93, -62.35) * mm});
            skPoint(sketch, "E23.middle", {"position": v(49.25, -61.1) * mm});
            skCircle(sketch, "E24", {"center": v(49.25, -61.1) * mm, "radius": 0.62 * mm});
            skCircle(sketch, "E25.1.0.0", {"center": v(51.79, -61.1) * mm, "radius": 0.62 * mm});
            skCircle(sketch, "E25.2.0.0", {"center": v(54.33, -61.1) * mm, "radius": 0.62 * mm});
            skCircle(sketch, "E25.3.0.0", {"center": v(56.87, -61.1) * mm, "radius": 0.62 * mm});
            skCircle(sketch, "E25.4.0.0", {"center": v(59.4, -61.1) * mm, "radius": 0.62 * mm});
            skLineSegment(sketch, "E25.direction1", {"start": v(49.25, -61.1) * mm, "end": v(51.79, -61.1) * mm, "construction": true});
            skLineSegment(sketch, "E26.bottom", {"start": v(48, -68.7) * mm, "end": v(78.99, -68.7) * mm});
            skLineSegment(sketch, "E26.top", {"start": v(48, -71.2) * mm, "end": v(78.99, -71.2) * mm});
            skLineSegment(sketch, "E26.left", {"start": v(48, -68.7) * mm, "end": v(48, -71.2) * mm});
            skLineSegment(sketch, "E26.right", {"start": v(78.99, -68.7) * mm, "end": v(78.99, -71.2) * mm});
            skCircle(sketch, "E27", {"center": v(49.53, -69.95) * mm, "radius": 0.63 * mm});
            skCircle(sketch, "E28.1.0.0", {"center": v(52.07, -69.95) * mm, "radius": 0.63 * mm});
            skCircle(sketch, "E28.2.0.0", {"center": v(54.6, -69.95) * mm, "radius": 0.63 * mm});
            skCircle(sketch, "E28.3.0.0", {"center": v(57.15, -69.95) * mm, "radius": 0.63 * mm});
            skCircle(sketch, "E28.4.0.0", {"center": v(59.69, -69.95) * mm, "radius": 0.63 * mm});
            skCircle(sketch, "E28.5.0.0", {"center": v(62.23, -69.95) * mm, "radius": 0.63 * mm});
            skCircle(sketch, "E28.6.0.0", {"center": v(64.77, -69.95) * mm, "radius": 0.63 * mm});
            skCircle(sketch, "E28.7.0.0", {"center": v(67.3, -69.95) * mm, "radius": 0.63 * mm});
            skCircle(sketch, "E28.8.0.0", {"center": v(69.85, -69.95) * mm, "radius": 0.63 * mm});
            skCircle(sketch, "E28.9.0.0", {"center": v(72.39, -69.95) * mm, "radius": 0.63 * mm});
            skCircle(sketch, "E28.10.0.0", {"center": v(74.93, -69.95) * mm, "radius": 0.63 * mm});
            skCircle(sketch, "E28.11.0.0", {"center": v(77.47, -69.95) * mm, "radius": 0.63 * mm});
            skLineSegment(sketch, "E28.direction1", {"start": v(49.53, -69.95) * mm, "end": v(52.07, -69.95) * mm, "construction": true});
            skLineSegment(sketch, "E29.bottom", {"start": v(49.13, -49.32) * mm, "end": v(64.87, -49.32) * mm});
            skLineSegment(sketch, "E29.top", {"start": v(49.13, -51.82) * mm, "end": v(64.87, -51.82) * mm});
            skLineSegment(sketch, "E29.left", {"start": v(49.13, -49.32) * mm, "end": v(49.13, -51.82) * mm});
            skLineSegment(sketch, "E29.right", {"start": v(64.87, -49.32) * mm, "end": v(64.87, -51.82) * mm});
            skCircle(sketch, "E30", {"center": v(50.65, -50.57) * mm, "radius": 0.62 * mm});
            skCircle(sketch, "E31.1.0.0", {"center": v(53.19, -50.57) * mm, "radius": 0.62 * mm});
            skCircle(sketch, "E31.2.0.0", {"center": v(55.73, -50.57) * mm, "radius": 0.62 * mm});
            skCircle(sketch, "E31.3.0.0", {"center": v(58.27, -50.57) * mm, "radius": 0.62 * mm});
            skCircle(sketch, "E31.4.0.0", {"center": v(60.8, -50.57) * mm, "radius": 0.62 * mm});
            skCircle(sketch, "E31.5.0.0", {"center": v(63.35, -50.57) * mm, "radius": 0.62 * mm});
            skLineSegment(sketch, "E31.direction1", {"start": v(50.65, -50.57) * mm, "end": v(53.19, -50.57) * mm, "construction": true});
            skCircle(sketch, "E32", {"center": v(38.78, -61) * mm, "radius": 0.63 * mm});
            skCircle(sketch, "E33.1.0.0", {"center": v(41.32, -61) * mm, "radius": 0.63 * mm});
            skLineSegment(sketch, "E33.direction1", {"start": v(38.78, -61) * mm, "end": v(41.32, -61) * mm, "construction": true});
            skCircle(sketch, "E34", {"center": v(38.83, -63.73) * mm, "radius": 0.62 * mm});
            skCircle(sketch, "E35.1.0.0", {"center": v(41.37, -63.73) * mm, "radius": 0.62 * mm});
            skLineSegment(sketch, "E35.direction1", {"start": v(38.83, -63.73) * mm, "end": v(41.37, -63.73) * mm, "construction": true});
            skLineSegment(sketch, "E36.bottom", {"start": v(49.3, -37.95) * mm, "end": v(90.44, -37.95) * mm});
            skLineSegment(sketch, "E36.top", {"start": v(49.3, -40.45) * mm, "end": v(90.44, -40.45) * mm});
            skLineSegment(sketch, "E36.left", {"start": v(49.3, -37.95) * mm, "end": v(49.3, -40.45) * mm});
            skLineSegment(sketch, "E36.right", {"start": v(90.44, -37.95) * mm, "end": v(90.44, -40.45) * mm});
            skCircle(sketch, "E37", {"center": v(50.82, -39.2) * mm, "radius": 0.67 * mm});
            skCircle(sketch, "E38.1.0.0", {"center": v(53.36, -39.2) * mm, "radius": 0.67 * mm});
            skCircle(sketch, "E38.2.0.0", {"center": v(55.9, -39.2) * mm, "radius": 0.67 * mm});
            skCircle(sketch, "E38.3.0.0", {"center": v(58.44, -39.2) * mm, "radius": 0.67 * mm});
            skCircle(sketch, "E38.4.0.0", {"center": v(60.98, -39.2) * mm, "radius": 0.67 * mm});
            skCircle(sketch, "E38.5.0.0", {"center": v(63.52, -39.2) * mm, "radius": 0.67 * mm});
            skCircle(sketch, "E38.6.0.0", {"center": v(66.06, -39.2) * mm, "radius": 0.67 * mm});
            skCircle(sketch, "E38.7.0.0", {"center": v(68.6, -39.2) * mm, "radius": 0.67 * mm});
            skCircle(sketch, "E38.8.0.0", {"center": v(71.14, -39.2) * mm, "radius": 0.67 * mm});
            skCircle(sketch, "E38.9.0.0", {"center": v(73.68, -39.2) * mm, "radius": 0.67 * mm});
            skCircle(sketch, "E38.10.0.0", {"center": v(76.22, -39.2) * mm, "radius": 0.67 * mm});
            skCircle(sketch, "E38.11.0.0", {"center": v(78.76, -39.2) * mm, "radius": 0.67 * mm});
            skCircle(sketch, "E38.12.0.0", {"center": v(81.3, -39.2) * mm, "radius": 0.67 * mm});
            skCircle(sketch, "E38.13.0.0", {"center": v(83.84, -39.2) * mm, "radius": 0.67 * mm});
            skCircle(sketch, "E38.14.0.0", {"center": v(86.38, -39.2) * mm, "radius": 0.67 * mm});
            skCircle(sketch, "E38.15.0.0", {"center": v(88.92, -39.2) * mm, "radius": 0.67 * mm});
            skLineSegment(sketch, "E38.direction1", {"start": v(50.82, -39.2) * mm, "end": v(53.36, -39.2) * mm, "construction": true});
            skSolve(sketch);
        }
        {
            var Q0;
            Q0=makeQuery(id+"F3.imprint","IMPRINT",FACE,{"disambiguationData":[TD([[makeQuery(id+"F3.imprint","IMPRINT",EDGE,{"derivedFrom":sQuery(id+"F3.wireOp",EDGE,"E16.bottom")}),-1.0]])]});
            extrude(context, id + "F4", {"entities" : qUnion([Q0]), "depth" : 8.5 * mm});
        }
        {
            var Q0;
            Q0=makeQuery(id+"F3.imprint","IMPRINT",FACE,{"disambiguationData":[TD([[makeQuery(id+"F3.imprint","IMPRINT",EDGE,{"derivedFrom":sQuery(id+"F3.wireOp",EDGE,"E20.bottom")}),-1.0]])]});
            var Q1;
            Q1=makeQuery(id+"F3.imprint","IMPRINT",FACE,{"disambiguationData":[TD([[makeQuery(id+"F3.imprint","IMPRINT",EDGE,{"derivedFrom":sQuery(id+"F3.wireOp",EDGE,"E19.bottom")}),-1.0]])]});
            var Q2;
            Q2=makeQuery(id+"F3.imprint","IMPRINT",FACE,{"disambiguationData":[TD([[makeQuery(id+"F3.imprint","IMPRINT",EDGE,{"derivedFrom":sQuery(id+"F3.wireOp",EDGE,"c27649e9-8674-45e7-bca4-547f7a5bf2d9.bottom")}),-1.0]])]});
            extrude(context, id + "F5", {"entities" : qUnion([Q0, Q1, Q2]), "depth" : 2 * mm});
        }
        {
            var Q0;
            Q0=qCreatedBy(makeId("Top.planeOp"),FACE);
            var sketch = newSketch(context, id + "F6", { "sketchPlane" : qUnion([Q0])});
            skLineSegment(sketch, "E39.bottom", {"start": v(7.42, 67.72) * mm, "end": v(44.42, 67.72) * mm});
            skLineSegment(sketch, "E39.top", {"start": v(7.42, 45.72) * mm, "end": v(44.42, 45.72) * mm});
            skLineSegment(sketch, "E39.left", {"start": v(7.42, 67.72) * mm, "end": v(7.42, 45.72) * mm});
            skLineSegment(sketch, "E39.right", {"start": v(44.42, 67.72) * mm, "end": v(44.42, 45.72) * mm});
            skCircle(sketch, "E40", {"center": v(17.42, 66.22) * mm, "radius": 0.75 * mm});
            skCircle(sketch, "E41.0", {"center": v(21.48, 23.01) * mm, "radius": 0.75 * mm});
            skCircle(sketch, "E42.1.0.0", {"center": v(19.96, 66.22) * mm, "radius": 0.75 * mm});
            skCircle(sketch, "E42.2.0.0", {"center": v(22.5, 66.22) * mm, "radius": 0.75 * mm});
            skCircle(sketch, "E42.3.0.0", {"center": v(25.04, 66.22) * mm, "radius": 0.75 * mm});
            skCircle(sketch, "E42.4.0.0", {"center": v(27.58, 66.22) * mm, "radius": 0.75 * mm});
            skCircle(sketch, "E42.5.0.0", {"center": v(30.12, 66.22) * mm, "radius": 0.75 * mm});
            skCircle(sketch, "E42.6.0.0", {"center": v(32.66, 66.22) * mm, "radius": 0.75 * mm});
            skCircle(sketch, "E42.7.0.0", {"center": v(35.2, 66.22) * mm, "radius": 0.75 * mm});
            skLineSegment(sketch, "E42.direction1", {"start": v(17.42, 66.22) * mm, "end": v(19.96, 66.22) * mm, "construction": true});
            skCircle(sketch, "E43.0", {"center": v(-34.4, 0) * mm, "radius": 1.5 * mm});
            skCircle(sketch, "E44", {"center": v(9.92, 65.22) * mm, "radius": 1.5 * mm});
            skCircle(sketch, "E45.0.1.0", {"center": v(9.92, 48.22) * mm, "radius": 1.5 * mm});
            skLineSegment(sketch, "E45.direction1", {"start": v(9.92, 65.22) * mm, "end": v(34.92, 65.22) * mm, "construction": true});
            skLineSegment(sketch, "E45.direction2", {"start": v(9.92, 65.22) * mm, "end": v(9.92, 48.22) * mm, "construction": true});
            skLineSegment(sketch, "E46.bottom", {"start": v(-59.16, 70.23) * mm, "end": v(-21.16, 70.23) * mm});
            skLineSegment(sketch, "E46.top", {"start": v(-59.16, 52.23) * mm, "end": v(-21.16, 52.23) * mm});
            skLineSegment(sketch, "E46.left", {"start": v(-59.16, 70.23) * mm, "end": v(-59.16, 52.23) * mm});
            skLineSegment(sketch, "E46.right", {"start": v(-21.16, 70.23) * mm, "end": v(-21.16, 52.23) * mm});
            skCircle(sketch, "E47", {"center": v(-53.16, 68.27) * mm, "radius": 0.75 * mm});
            skCircle(sketch, "E48.0.1.0", {"center": v(-53.16, 54.19) * mm, "radius": 0.75 * mm});
            skCircle(sketch, "E48.1.0.0", {"center": v(-50.62, 68.27) * mm, "radius": 0.75 * mm});
            skCircle(sketch, "E48.1.1.0", {"center": v(-50.62, 54.19) * mm, "radius": 0.75 * mm});
            skCircle(sketch, "E48.2.0.0", {"center": v(-48.08, 68.27) * mm, "radius": 0.75 * mm});
            skCircle(sketch, "E48.2.1.0", {"center": v(-48.08, 54.19) * mm, "radius": 0.75 * mm});
            skCircle(sketch, "E48.3.0.0", {"center": v(-45.54, 68.27) * mm, "radius": 0.75 * mm});
            skCircle(sketch, "E48.3.1.0", {"center": v(-45.54, 54.19) * mm, "radius": 0.75 * mm});
            skCircle(sketch, "E48.4.0.0", {"center": v(-43, 68.27) * mm, "radius": 0.75 * mm});
            skCircle(sketch, "E48.4.1.0", {"center": v(-43, 54.19) * mm, "radius": 0.75 * mm});
            skCircle(sketch, "E48.5.0.0", {"center": v(-40.46, 68.27) * mm, "radius": 0.75 * mm});
            skCircle(sketch, "E48.5.1.0", {"center": v(-40.46, 54.19) * mm, "radius": 0.75 * mm});
            skCircle(sketch, "E48.6.0.0", {"center": v(-37.92, 68.27) * mm, "radius": 0.75 * mm});
            skCircle(sketch, "E48.6.1.0", {"center": v(-37.92, 54.19) * mm, "radius": 0.75 * mm});
            skCircle(sketch, "E48.7.0.0", {"center": v(-35.38, 68.27) * mm, "radius": 0.75 * mm});
            skCircle(sketch, "E48.7.1.0", {"center": v(-35.38, 54.19) * mm, "radius": 0.75 * mm});
            skCircle(sketch, "E48.8.0.0", {"center": v(-32.84, 68.27) * mm, "radius": 0.75 * mm});
            skCircle(sketch, "E48.8.1.0", {"center": v(-32.84, 54.19) * mm, "radius": 0.75 * mm});
            skCircle(sketch, "E48.9.0.0", {"center": v(-30.3, 68.27) * mm, "radius": 0.75 * mm});
            skCircle(sketch, "E48.9.1.0", {"center": v(-30.3, 54.19) * mm, "radius": 0.75 * mm});
            skCircle(sketch, "E48.10.0.0", {"center": v(-27.76, 68.27) * mm, "radius": 0.75 * mm});
            skCircle(sketch, "E48.10.1.0", {"center": v(-27.76, 54.19) * mm, "radius": 0.75 * mm});
            skCircle(sketch, "E48.11.0.0", {"center": v(-25.22, 68.27) * mm, "radius": 0.75 * mm});
            skCircle(sketch, "E48.11.1.0", {"center": v(-25.22, 54.19) * mm, "radius": 0.75 * mm});
            skLineSegment(sketch, "E48.direction1", {"start": v(-53.16, 68.27) * mm, "end": v(-50.62, 68.27) * mm, "construction": true});
            skLineSegment(sketch, "E48.direction2", {"start": v(-53.16, 68.27) * mm, "end": v(-53.16, 54.19) * mm, "construction": true});
            skCircle(sketch, "E49", {"center": v(-56.66, 67.73) * mm, "radius": 1.5 * mm});
            skCircle(sketch, "E50.0.1.0", {"center": v(-56.66, 54.73) * mm, "radius": 1.5 * mm});
            skLineSegment(sketch, "E50.direction1", {"start": v(-56.66, 67.73) * mm, "end": v(-31.66, 67.73) * mm, "construction": true});
            skLineSegment(sketch, "E50.direction2", {"start": v(-56.66, 67.73) * mm, "end": v(-56.66, 54.73) * mm, "construction": true});
            skCircle(sketch, "E51", {"center": v(-22.8, 67.27) * mm, "radius": 0.75 * mm});
            skCircle(sketch, "E52.0.1.0", {"center": v(-22.8, 64.73) * mm, "radius": 0.75 * mm});
            skCircle(sketch, "E52.0.2.0", {"center": v(-22.8, 62.2) * mm, "radius": 0.75 * mm});
            skCircle(sketch, "E52.0.3.0", {"center": v(-22.8, 59.65) * mm, "radius": 0.75 * mm});
            skCircle(sketch, "E52.0.4.0", {"center": v(-22.8, 57.11) * mm, "radius": 0.75 * mm});
            skLineSegment(sketch, "E52.direction1", {"start": v(-22.8, 67.27) * mm, "end": v(2.2, 67.27) * mm, "construction": true});
            skLineSegment(sketch, "E52.direction2", {"start": v(-22.8, 67.27) * mm, "end": v(-22.8, 64.73) * mm, "construction": true});
            skCircle(sketch, "E53.0.0.5", {"center": v(-22.8, 54.57) * mm, "radius": 0.75 * mm});
            skLineSegment(sketch, "E54.bottom", {"start": v(-58.08, -39.65) * mm, "end": v(0, -39.65) * mm});
            skLineSegment(sketch, "E54.top", {"start": v(-58.08, -67.37) * mm, "end": v(0, -67.37) * mm});
            skLineSegment(sketch, "E54.left", {"start": v(-58.08, -39.65) * mm, "end": v(-58.08, -67.37) * mm});
            skLineSegment(sketch, "E54.right", {"start": v(0, -39.65) * mm, "end": v(0, -67.37) * mm});
            skCircle(sketch, "E55", {"center": v(-50.08, -41.15) * mm, "radius": 0.75 * mm});
            skCircle(sketch, "E56.0.1.0", {"center": v(-50.08, -65.39) * mm, "radius": 0.75 * mm});
            skCircle(sketch, "E56.1.0.0", {"center": v(-47.54, -41.15) * mm, "radius": 0.75 * mm});
            skCircle(sketch, "E56.1.1.0", {"center": v(-47.54, -65.39) * mm, "radius": 0.75 * mm});
            skCircle(sketch, "E56.2.0.0", {"center": v(-45, -41.15) * mm, "radius": 0.75 * mm});
            skCircle(sketch, "E56.2.1.0", {"center": v(-45, -65.39) * mm, "radius": 0.75 * mm});
            skCircle(sketch, "E56.3.0.0", {"center": v(-42.46, -41.15) * mm, "radius": 0.75 * mm});
            skCircle(sketch, "E56.3.1.0", {"center": v(-42.46, -65.39) * mm, "radius": 0.75 * mm});
            skCircle(sketch, "E56.4.0.0", {"center": v(-39.92, -41.15) * mm, "radius": 0.75 * mm});
            skCircle(sketch, "E56.4.1.0", {"center": v(-39.92, -65.39) * mm, "radius": 0.75 * mm});
            skCircle(sketch, "E56.5.0.0", {"center": v(-37.38, -41.15) * mm, "radius": 0.75 * mm});
            skCircle(sketch, "E56.5.1.0", {"center": v(-37.38, -65.39) * mm, "radius": 0.75 * mm});
            skCircle(sketch, "E56.6.0.0", {"center": v(-34.84, -41.15) * mm, "radius": 0.75 * mm});
            skCircle(sketch, "E56.6.1.0", {"center": v(-34.84, -65.39) * mm, "radius": 0.75 * mm});
            skCircle(sketch, "E56.7.0.0", {"center": v(-32.3, -41.15) * mm, "radius": 0.75 * mm});
            skCircle(sketch, "E56.7.1.0", {"center": v(-32.3, -65.39) * mm, "radius": 0.75 * mm});
            skCircle(sketch, "E56.8.0.0", {"center": v(-29.76, -41.15) * mm, "radius": 0.75 * mm});
            skCircle(sketch, "E56.8.1.0", {"center": v(-29.76, -65.39) * mm, "radius": 0.75 * mm});
            skCircle(sketch, "E56.9.0.0", {"center": v(-27.22, -41.15) * mm, "radius": 0.75 * mm});
            skCircle(sketch, "E56.9.1.0", {"center": v(-27.22, -65.39) * mm, "radius": 0.75 * mm});
            skCircle(sketch, "E56.10.0.0", {"center": v(-24.68, -41.15) * mm, "radius": 0.75 * mm});
            skCircle(sketch, "E56.10.1.0", {"center": v(-24.68, -65.39) * mm, "radius": 0.75 * mm});
            skCircle(sketch, "E56.11.0.0", {"center": v(-22.14, -41.15) * mm, "radius": 0.75 * mm});
            skCircle(sketch, "E56.11.1.0", {"center": v(-22.14, -65.39) * mm, "radius": 0.75 * mm});
            skCircle(sketch, "E56.12.0.0", {"center": v(-19.6, -41.15) * mm, "radius": 0.75 * mm});
            skCircle(sketch, "E56.12.1.0", {"center": v(-19.6, -65.39) * mm, "radius": 0.75 * mm});
            skCircle(sketch, "E56.13.0.0", {"center": v(-17.06, -41.15) * mm, "radius": 0.75 * mm});
            skCircle(sketch, "E56.13.1.0", {"center": v(-17.06, -65.39) * mm, "radius": 0.75 * mm});
            skCircle(sketch, "E56.14.0.0", {"center": v(-14.52, -41.15) * mm, "radius": 0.75 * mm});
            skCircle(sketch, "E56.14.1.0", {"center": v(-14.52, -65.39) * mm, "radius": 0.75 * mm});
            skCircle(sketch, "E56.15.0.0", {"center": v(-11.98, -41.15) * mm, "radius": 0.75 * mm});
            skCircle(sketch, "E56.15.1.0", {"center": v(-11.98, -65.39) * mm, "radius": 0.75 * mm});
            skLineSegment(sketch, "E56.direction1", {"start": v(-50.08, -41.15) * mm, "end": v(-47.54, -41.15) * mm, "construction": true});
            skLineSegment(sketch, "E56.direction2", {"start": v(-50.08, -41.15) * mm, "end": v(-50.08, -65.39) * mm, "construction": true});
            skLineSegment(sketch, "E57.bottom", {"start": v(-15.2, 117.58) * mm, "end": v(6, 117.58) * mm});
            skLineSegment(sketch, "E57.top", {"start": v(-15.2, 99.58) * mm, "end": v(6, 99.58) * mm});
            skLineSegment(sketch, "E57.left", {"start": v(-15.2, 117.58) * mm, "end": v(-15.2, 99.58) * mm});
            skLineSegment(sketch, "E57.right", {"start": v(6, 117.58) * mm, "end": v(6, 99.58) * mm});
            skCircle(sketch, "E58", {"center": v(3.97, 113.66) * mm, "radius": 0.75 * mm});
            skCircle(sketch, "E59.0.1.0", {"center": v(3.97, 111.12) * mm, "radius": 0.75 * mm});
            skCircle(sketch, "E59.0.2.0", {"center": v(3.97, 108.58) * mm, "radius": 0.75 * mm});
            skCircle(sketch, "E59.0.3.0", {"center": v(3.97, 106.04) * mm, "radius": 0.75 * mm});
            skCircle(sketch, "E59.0.4.0", {"center": v(3.97, 103.5) * mm, "radius": 0.75 * mm});
            skLineSegment(sketch, "E59.direction1", {"start": v(3.97, 113.66) * mm, "end": v(28.97, 113.66) * mm, "construction": true});
            skLineSegment(sketch, "E59.direction2", {"start": v(3.97, 113.66) * mm, "end": v(3.97, 111.12) * mm, "construction": true});
            skLineSegment(sketch, "E60.bottom", {"start": v(-87, 117.69) * mm, "end": v(-61.5, 117.69) * mm});
            skLineSegment(sketch, "E60.top", {"start": v(-87, 97.69) * mm, "end": v(-61.5, 97.69) * mm});
            skLineSegment(sketch, "E60.left", {"start": v(-87, 117.69) * mm, "end": v(-87, 97.69) * mm});
            skLineSegment(sketch, "E60.right", {"start": v(-61.5, 117.69) * mm, "end": v(-61.5, 97.69) * mm});
            skCircle(sketch, "E61", {"center": v(-80.6, 99.19) * mm, "radius": 0.75 * mm});
            skCircle(sketch, "E62.1.0.0", {"center": v(-78.06, 99.19) * mm, "radius": 0.75 * mm});
            skCircle(sketch, "E62.2.0.0", {"center": v(-75.52, 99.19) * mm, "radius": 0.75 * mm});
            skCircle(sketch, "E62.3.0.0", {"center": v(-72.98, 99.19) * mm, "radius": 0.75 * mm});
            skCircle(sketch, "E62.4.0.0", {"center": v(-70.44, 99.19) * mm, "radius": 0.75 * mm});
            skLineSegment(sketch, "E62.direction1", {"start": v(-80.6, 99.19) * mm, "end": v(-78.06, 99.19) * mm, "construction": true});
            skCircle(sketch, "E63.0.5.0", {"center": v(-67.9, 99.19) * mm, "radius": 0.75 * mm});
            skCircle(sketch, "E64", {"center": v(54.53, 63.93) * mm, "radius": 0.75 * mm});
            skCircle(sketch, "E65.0.1.0", {"center": v(54.53, 44.77) * mm, "radius": 0.75 * mm});
            skCircle(sketch, "E65.1.0.0", {"center": v(57.07, 63.93) * mm, "radius": 0.75 * mm});
            skCircle(sketch, "E65.1.1.0", {"center": v(57.07, 44.77) * mm, "radius": 0.75 * mm});
            skCircle(sketch, "E65.2.0.0", {"center": v(59.61, 63.93) * mm, "radius": 0.75 * mm});
            skCircle(sketch, "E65.2.1.0", {"center": v(59.61, 44.77) * mm, "radius": 0.75 * mm});
            skCircle(sketch, "E65.3.0.0", {"center": v(62.15, 63.93) * mm, "radius": 0.75 * mm});
            skCircle(sketch, "E65.3.1.0", {"center": v(62.15, 44.77) * mm, "radius": 0.75 * mm});
            skCircle(sketch, "E65.4.0.0", {"center": v(64.7, 63.93) * mm, "radius": 0.75 * mm});
            skCircle(sketch, "E65.4.1.0", {"center": v(64.7, 44.77) * mm, "radius": 0.75 * mm});
            skCircle(sketch, "E65.5.0.0", {"center": v(67.23, 63.93) * mm, "radius": 0.75 * mm});
            skCircle(sketch, "E65.5.1.0", {"center": v(67.23, 44.77) * mm, "radius": 0.75 * mm});
            skCircle(sketch, "E65.6.0.0", {"center": v(69.77, 63.93) * mm, "radius": 0.75 * mm});
            skCircle(sketch, "E65.6.1.0", {"center": v(69.77, 44.77) * mm, "radius": 0.75 * mm});
            skCircle(sketch, "E65.7.0.0", {"center": v(72.31, 63.93) * mm, "radius": 0.75 * mm});
            skCircle(sketch, "E65.7.1.0", {"center": v(72.31, 44.77) * mm, "radius": 0.75 * mm});
            skCircle(sketch, "E65.8.0.0", {"center": v(74.85, 63.93) * mm, "radius": 0.75 * mm});
            skCircle(sketch, "E65.8.1.0", {"center": v(74.85, 44.77) * mm, "radius": 0.75 * mm});
            skCircle(sketch, "E65.9.0.0", {"center": v(77.4, 63.93) * mm, "radius": 0.75 * mm});
            skCircle(sketch, "E65.9.1.0", {"center": v(77.4, 44.77) * mm, "radius": 0.75 * mm});
            skCircle(sketch, "E65.10.0.0", {"center": v(79.93, 63.93) * mm, "radius": 0.75 * mm});
            skCircle(sketch, "E65.10.1.0", {"center": v(79.93, 44.77) * mm, "radius": 0.75 * mm});
            skCircle(sketch, "E65.11.0.0", {"center": v(82.47, 63.93) * mm, "radius": 0.75 * mm});
            skCircle(sketch, "E65.11.1.0", {"center": v(82.47, 44.77) * mm, "radius": 0.75 * mm});
            skLineSegment(sketch, "E65.direction1", {"start": v(54.53, 63.93) * mm, "end": v(57.07, 63.93) * mm, "construction": true});
            skLineSegment(sketch, "E65.direction2", {"start": v(54.53, 63.93) * mm, "end": v(54.53, 44.77) * mm, "construction": true});
            skLineSegment(sketch, "E66.bottom", {"start": v(53.03, 65.43) * mm, "end": v(83.97, 65.43) * mm});
            skLineSegment(sketch, "E66.top", {"start": v(53.03, 43.27) * mm, "end": v(83.97, 43.27) * mm});
            skLineSegment(sketch, "E66.left", {"start": v(53.03, 65.43) * mm, "end": v(53.03, 43.27) * mm});
            skLineSegment(sketch, "E66.right", {"start": v(83.97, 65.43) * mm, "end": v(83.97, 43.27) * mm});
            skSolve(sketch);
        }
        {
            var Q0;
            Q0=makeQuery(id+"F6.imprint","IMPRINT",FACE,{"disambiguationData":[TD([[makeQuery(id+"F6.imprint","IMPRINT",EDGE,{"derivedFrom":sQuery(id+"F6.wireOp",EDGE,"E39.bottom")}),-1.0]])]});
            extrude(context, id + "F7", {"entities" : qUnion([Q0]), "depth" : 2 * mm});
        }
        {
            var Q0;
            Q0=makeQuery(id+"F7.opExtrude","SWEPT_EDGE",EDGE,{"disambiguationData":[OSD([sQuery(id+"F6.wireOp",EDGE,"E39.bottom"),sQuery(id+"F6.wireOp",EDGE,"E39.right")])]});
            var Q1;
            Q1=makeQuery(id+"F7.opExtrude","SWEPT_EDGE",EDGE,{"disambiguationData":[OSD([sQuery(id+"F6.wireOp",EDGE,"E39.top"),sQuery(id+"F6.wireOp",EDGE,"E39.right")])]});
            var Q2;
            Q2=makeQuery(id+"F7.opExtrude","SWEPT_EDGE",EDGE,{"disambiguationData":[OSD([sQuery(id+"F6.wireOp",EDGE,"E39.bottom"),sQuery(id+"F6.wireOp",EDGE,"E39.left")])]});
            var Q3;
            Q3=makeQuery(id+"F7.opExtrude","SWEPT_EDGE",EDGE,{"disambiguationData":[OSD([sQuery(id+"F6.wireOp",EDGE,"E39.top"),sQuery(id+"F6.wireOp",EDGE,"E39.left")])]});
            fillet(context, id + "F8", {"entities" : qUnion([Q0, Q1, Q2, Q3]), "radius" : 2.5 * mm, "tangentPropagation" : true, "allowEdgeOverflow" : false});
        }
        {
            var Q0;
            Q0=makeQuery(id+"F3.imprint","IMPRINT",FACE,{"disambiguationData":[TD([[makeQuery(id+"F3.imprint","IMPRINT",EDGE,{"derivedFrom":sQuery(id+"F3.wireOp",EDGE,"E22.bottom")}),-1.0]])]});
            extrude(context, id + "F9", {"entities" : qUnion([Q0]), "depth" : 8.5 * mm});
        }
        {
            var Q0;
            Q0=makeQuery(id+"F6.imprint","IMPRINT",FACE,{"disambiguationData":[TD([[makeQuery(id+"F6.imprint","IMPRINT",EDGE,{"derivedFrom":sQuery(id+"F6.wireOp",EDGE,"E46.bottom")}),-1.0]])]});
            extrude(context, id + "F10", {"entities" : qUnion([Q0]), "depth" : 2 * mm});
        }
        {
            var Q0;
            Q0=makeQuery(id+"F10.opExtrude","SWEPT_EDGE",EDGE,{"disambiguationData":[OSD([sQuery(id+"F6.wireOp",EDGE,"E46.bottom"),sQuery(id+"F6.wireOp",EDGE,"E46.left")])]});
            var Q1;
            Q1=makeQuery(id+"F10.opExtrude","SWEPT_EDGE",EDGE,{"disambiguationData":[OSD([sQuery(id+"F6.wireOp",EDGE,"E46.top"),sQuery(id+"F6.wireOp",EDGE,"E46.left")])]});
            fillet(context, id + "F11", {"entities" : qUnion([Q0, Q1]), "radius" : 2.5 * mm, "tangentPropagation" : true, "allowEdgeOverflow" : false});
        }
        {
            var Q0;
            Q0=makeQuery(id+"F3.imprint","IMPRINT",FACE,{"disambiguationData":[TD([[makeQuery(id+"F3.imprint","IMPRINT",EDGE,{"derivedFrom":sQuery(id+"F3.wireOp",EDGE,"E26.bottom")}),-1.0]])]});
            extrude(context, id + "F12", {"entities" : qUnion([Q0]), "depth" : 8.5 * mm});
        }
        {
            var Q0;
            Q0=makeQuery(id+"F6.imprint","IMPRINT",FACE,{"disambiguationData":[TD([[makeQuery(id+"F6.imprint","IMPRINT",EDGE,{"derivedFrom":sQuery(id+"F6.wireOp",EDGE,"E54.bottom")}),-1.0]])]});
            extrude(context, id + "F13", {"entities" : qUnion([Q0]), "depth" : 2 * mm});
        }
        {
            var Q0;
            Q0=makeQuery(id+"F13.opExtrude","SWEPT_EDGE",EDGE,{"disambiguationData":[OSD([sQuery(id+"F6.wireOp",EDGE,"E54.bottom"),sQuery(id+"F6.wireOp",EDGE,"E54.left")])]});
            var Q1;
            Q1=makeQuery(id+"F13.opExtrude","SWEPT_EDGE",EDGE,{"disambiguationData":[OSD([sQuery(id+"F6.wireOp",EDGE,"E54.bottom"),sQuery(id+"F6.wireOp",EDGE,"E54.right")])]});
            var Q2;
            Q2=makeQuery(id+"F13.opExtrude","SWEPT_EDGE",EDGE,{"disambiguationData":[OSD([sQuery(id+"F6.wireOp",EDGE,"E54.top"),sQuery(id+"F6.wireOp",EDGE,"E54.right")])]});
            var Q3;
            Q3=makeQuery(id+"F13.opExtrude","SWEPT_EDGE",EDGE,{"disambiguationData":[OSD([sQuery(id+"F6.wireOp",EDGE,"E54.top"),sQuery(id+"F6.wireOp",EDGE,"E54.left")])]});
            fillet(context, id + "F14", {"entities" : qUnion([Q0, Q1, Q2, Q3]), "radius" : 2.54 * mm, "tangentPropagation" : true, "allowEdgeOverflow" : false});
        }
        {
            var Q0;
            Q0=makeQuery(id+"F6.imprint","IMPRINT",FACE,{"disambiguationData":[TD([[makeQuery(id+"F6.imprint","IMPRINT",EDGE,{"derivedFrom":sQuery(id+"F6.wireOp",EDGE,"E57.bottom")}),-1.0]])]});
            extrude(context, id + "F15", {"entities" : qUnion([Q0]), "depth" : 2 * mm});
        }
        {
            var Q0;
            Q0=makeQuery(id+"F15.opExtrude","SWEPT_EDGE",EDGE,{"disambiguationData":[OSD([sQuery(id+"F6.wireOp",EDGE,"E57.bottom"),sQuery(id+"F6.wireOp",EDGE,"E57.left")])]});
            var Q1;
            Q1=makeQuery(id+"F15.opExtrude","SWEPT_EDGE",EDGE,{"disambiguationData":[OSD([sQuery(id+"F6.wireOp",EDGE,"E57.bottom"),sQuery(id+"F6.wireOp",EDGE,"E57.right")])]});
            var Q2;
            Q2=makeQuery(id+"F15.opExtrude","SWEPT_EDGE",EDGE,{"disambiguationData":[OSD([sQuery(id+"F6.wireOp",EDGE,"E57.top"),sQuery(id+"F6.wireOp",EDGE,"E57.right")])]});
            var Q3;
            Q3=makeQuery(id+"F15.opExtrude","SWEPT_EDGE",EDGE,{"disambiguationData":[OSD([sQuery(id+"F6.wireOp",EDGE,"E57.top"),sQuery(id+"F6.wireOp",EDGE,"E57.left")])]});
            fillet(context, id + "F16", {"entities" : qUnion([Q0, Q1, Q2, Q3]), "radius" : 2.5 * mm, "tangentPropagation" : true, "allowEdgeOverflow" : false});
        }
        {
            var Q0;
            Q0=makeQuery(id+"F6.imprint","IMPRINT",FACE,{"disambiguationData":[TD([[makeQuery(id+"F6.imprint","IMPRINT",EDGE,{"derivedFrom":sQuery(id+"F6.wireOp",EDGE,"E60.bottom")}),-1.0]])]});
            extrude(context, id + "F17", {"entities" : qUnion([Q0]), "depth" : 4 * mm});
        }
        {
            var Q0;
            Q0=makeQuery(id+"F17.opExtrude","SWEPT_EDGE",EDGE,{"disambiguationData":[OSD([sQuery(id+"F6.wireOp",EDGE,"E60.bottom"),sQuery(id+"F6.wireOp",EDGE,"E60.left")])]});
            var Q1;
            Q1=makeQuery(id+"F17.opExtrude","SWEPT_EDGE",EDGE,{"disambiguationData":[OSD([sQuery(id+"F6.wireOp",EDGE,"E60.bottom"),sQuery(id+"F6.wireOp",EDGE,"E60.right")])]});
            var Q2;
            Q2=makeQuery(id+"F17.opExtrude","SWEPT_EDGE",EDGE,{"disambiguationData":[OSD([sQuery(id+"F6.wireOp",EDGE,"E60.top"),sQuery(id+"F6.wireOp",EDGE,"E60.right")])]});
            var Q3;
            Q3=makeQuery(id+"F17.opExtrude","SWEPT_EDGE",EDGE,{"disambiguationData":[OSD([sQuery(id+"F6.wireOp",EDGE,"E60.top"),sQuery(id+"F6.wireOp",EDGE,"E60.left")])]});
            fillet(context, id + "F18", {"entities" : qUnion([Q0, Q1, Q2, Q3]), "radius" : 2.5 * mm, "tangentPropagation" : true, "allowEdgeOverflow" : false});
        }
        {
            var Q0;
            Q0=makeQuery(id+"F6.imprint","IMPRINT",FACE,{"disambiguationData":[TD([[makeQuery(id+"F6.imprint","IMPRINT",EDGE,{"derivedFrom":sQuery(id+"F6.wireOp",EDGE,"E64")}),-1.0]])]});
            extrude(context, id + "F19", {"entities" : qUnion([Q0]), "depth" : 2 * mm});
        }
        {
            var Q0;
            Q0=makeQuery(id+"F3.imprint","IMPRINT",FACE,{"disambiguationData":[TD([[makeQuery(id+"F3.imprint","IMPRINT",EDGE,{"derivedFrom":sQuery(id+"F3.wireOp",EDGE,"E29.bottom")}),-1.0]])]});
            extrude(context, id + "F20", {"entities" : qUnion([Q0]), "depth" : 8.5 * mm});
        }
        {
            var Q0;
            Q0=makeQuery(id+"F3.imprint","IMPRINT",FACE,{"disambiguationData":[TD([[makeQuery(id+"F3.imprint","IMPRINT",EDGE,{"derivedFrom":sQuery(id+"F3.wireOp",EDGE,"E34")}),1.0]])]});
            var Q1;
            Q1=makeQuery(id+"F3.imprint","IMPRINT",FACE,{"disambiguationData":[TD([[makeQuery(id+"F3.imprint","IMPRINT",EDGE,{"derivedFrom":sQuery(id+"F3.wireOp",EDGE,"E35.1.0.0")}),1.0]])]});
            extrude(context, id + "F21", {"entities" : qUnion([Q0, Q1]), "operationType" : NewBodyOperationType.ADD, "depth" : 8 * mm});
        }
        {
            var Q0;
            Q0=makeQuery(id+"F3.imprint","IMPRINT",FACE,{"disambiguationData":[TD([[makeQuery(id+"F3.imprint","IMPRINT",EDGE,{"derivedFrom":sQuery(id+"F3.wireOp",EDGE,"E36.bottom")}),-1.0]])]});
            extrude(context, id + "F22", {"entities" : qUnion([Q0]), "depth" : 8.5 * mm});
        }
    });
